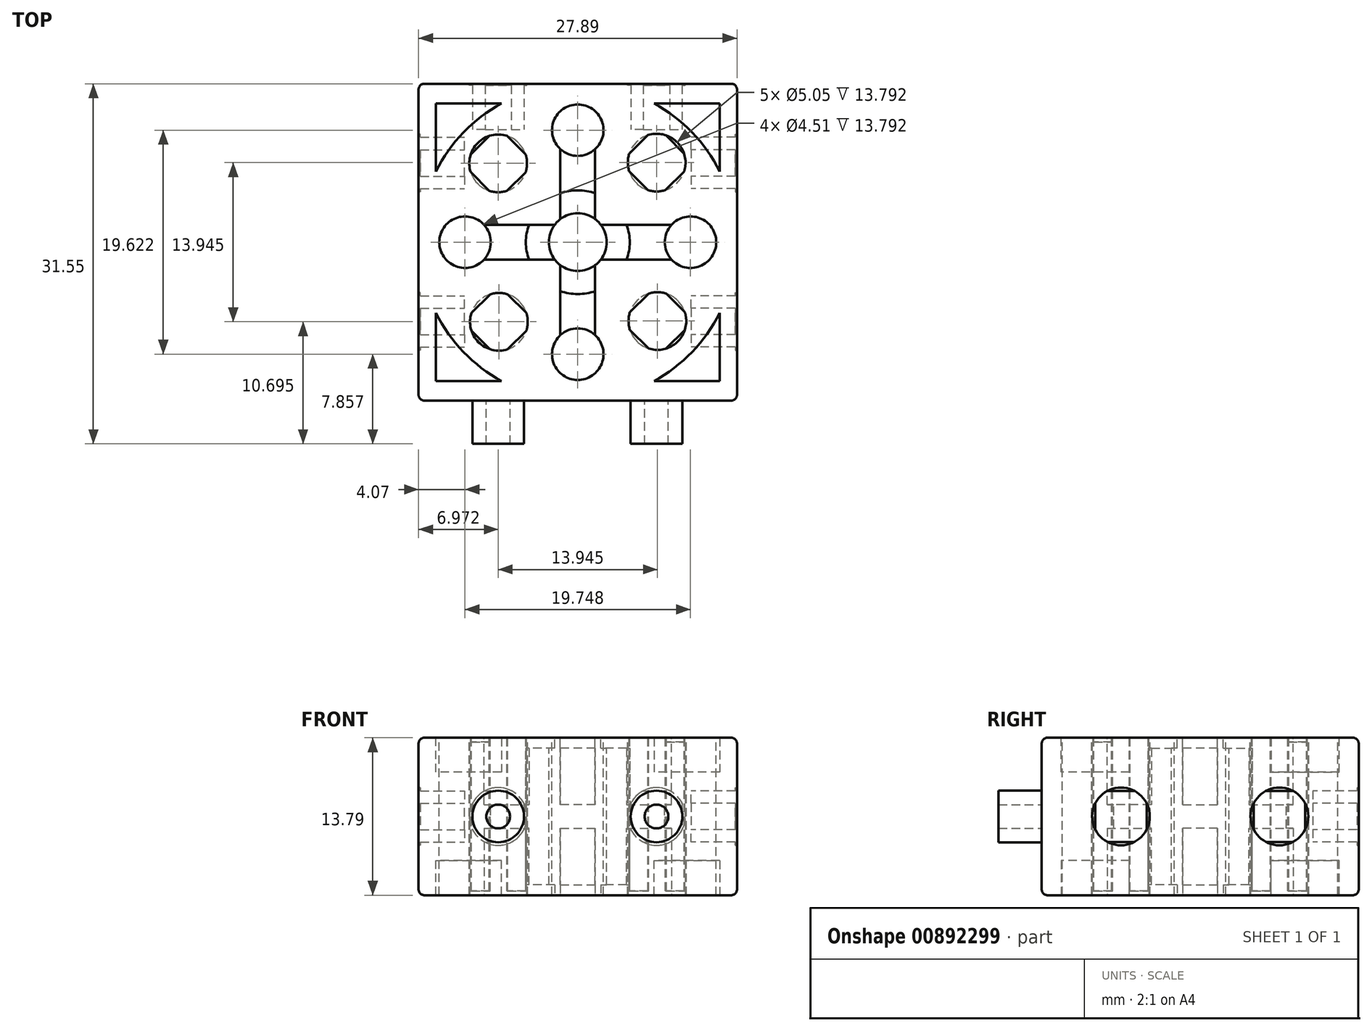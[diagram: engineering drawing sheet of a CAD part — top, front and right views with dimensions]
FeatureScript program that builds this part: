
annotation { "Feature Type Name" : "Feature", "Feature Type Description" : "" }
export const myFeature = defineFeature(function(context is Context, id is Id, definition is map)
    precondition{}
    {
        {
            var Q0;
            Q0=qCreatedBy(makeId("Top.planeOp"),FACE);
            var sketch = newSketch(context, id + "F0", { "sketchPlane" : qUnion([Q0])});
            skLineSegment(sketch, "E0.bottom", {"start": v(-12.61, 9.27) * mm, "end": v(15.28, 9.27) * mm});
            skLineSegment(sketch, "E0.top", {"start": v(-12.61, -18.5) * mm, "end": v(15.28, -18.5) * mm});
            skLineSegment(sketch, "E0.left", {"start": v(-12.61, 9.27) * mm, "end": v(-12.61, -18.5) * mm});
            skLineSegment(sketch, "E0.right", {"start": v(15.28, 9.27) * mm, "end": v(15.28, -18.5) * mm});
            skSolve(sketch);
        }
        {
            var Q0;
            Q0=qSketchRegion(id+"F0",true);
            extrude(context, id + "F1", {"entities" : qUnion([Q0]), "depth" : 13.8 * mm, "offsetDistance" : 25.4 * mm});
        }
        {
            var Q0;
            Q0=makeQuery(id+"F1.opExtrude","CAP_FACE",FACE,{"disambiguationData":[OSD([sQuery(id+"F0.wireOp",EDGE,"E0.bottom"),sQuery(id+"F0.wireOp",EDGE,"E0.top"),sQuery(id+"F0.wireOp",EDGE,"E0.left"),sQuery(id+"F0.wireOp",EDGE,"E0.right")])],"isStart":false});
            var sketch = newSketch(context, id + "F2", { "sketchPlane" : qUnion([Q0])});
            skLineSegment(sketch, "E1", {"start": v(1.33, 9.27) * mm, "end": v(1.33, -18.5) * mm, "construction": true});
            skLineSegment(sketch, "E2", {"start": v(-12.61, -4.61) * mm, "end": v(15.28, -4.61) * mm, "construction": true});
            skLineSegment(sketch, "E3.bottom", {"start": v(13.75, 7.56) * mm, "end": v(-11.09, 7.56) * mm});
            skLineSegment(sketch, "E3.top", {"start": v(13.75, -16.78) * mm, "end": v(-11.09, -16.78) * mm});
            skLineSegment(sketch, "E3.left", {"start": v(13.75, 7.56) * mm, "end": v(13.75, -16.78) * mm});
            skLineSegment(sketch, "E3.right", {"start": v(-11.09, 7.56) * mm, "end": v(-11.09, -16.78) * mm});
            skPoint(sketch, "E3.middle", {"position": v(1.33, -4.61) * mm});
            skSolve(sketch);
        }
        {
            var Q0;
            Q0=qSketchRegion(id+"F2",true);
            extrude(context, id + "F3", {"entities" : qUnion([Q0]), "operationType" : NewBodyOperationType.REMOVE, "oppositeDirection" : true, "depth" : 3.02 * mm, "offsetDistance" : 25.4 * mm});
        }
        {
            var Q0;
            Q0=makeQuery(id+"F1.opExtrude","CAP_FACE",FACE,{"disambiguationData":[OSD([sQuery(id+"F0.wireOp",EDGE,"E0.bottom"),sQuery(id+"F0.wireOp",EDGE,"E0.top"),sQuery(id+"F0.wireOp",EDGE,"E0.left"),sQuery(id+"F0.wireOp",EDGE,"E0.right")])],"isStart":true});
            var sketch = newSketch(context, id + "F4", { "sketchPlane" : qUnion([Q0])});
            skLineSegment(sketch, "E4.bottom", {"start": v(-11.09, -7.56) * mm, "end": v(13.75, -7.56) * mm});
            skLineSegment(sketch, "E4.top", {"start": v(-11.09, 16.78) * mm, "end": v(13.75, 16.78) * mm});
            skLineSegment(sketch, "E4.left", {"start": v(-11.09, -7.56) * mm, "end": v(-11.09, 16.78) * mm});
            skLineSegment(sketch, "E4.right", {"start": v(13.75, -7.56) * mm, "end": v(13.75, 16.78) * mm});
            skSolve(sketch);
        }
        {
            var Q0;
            Q0=makeQuery(id+"F4.imprint","IMPRINT",FACE,{"disambiguationData":[TD([[makeQuery(id+"F4.imprint","IMPRINT",EDGE,{"derivedFrom":sQuery(id+"F4.wireOp",EDGE,"E4.bottom")}),1.0]])]});
            extrude(context, id + "F5", {"entities" : qUnion([Q0]), "operationType" : NewBodyOperationType.REMOVE, "oppositeDirection" : true, "depth" : 3.02 * mm, "offsetDistance" : 25.4 * mm});
        }
        {
            var Q0;
            Q0=makeQuery(id+"F5.boolean.opBoolean","COPY",FACE,{"derivedFrom":makeQuery(id+"F5.opExtrude","CAP_FACE",FACE,{"disambiguationData":[OSD([sQuery(id+"F4.wireOp",EDGE,"E4.bottom"),sQuery(id+"F4.wireOp",EDGE,"E4.top"),sQuery(id+"F4.wireOp",EDGE,"E4.left"),sQuery(id+"F4.wireOp",EDGE,"E4.right")])],"isStart":false})});
            var sketch = newSketch(context, id + "F6", { "sketchPlane" : qUnion([Q0])});
            skCircle(sketch, "E5", {"center": v(1.33, 4.61) * mm, "radius": 13.88 * mm});
            skLineSegment(sketch, "E6", {"start": v(1.33, -7.56) * mm, "end": v(1.33, 16.78) * mm, "construction": true});
            skPoint(sketch, "E6.startSnap0", {"position": v(1.33, -7.56) * mm});
            skSolve(sketch);
        }
        {
            var Q0;
            {var subQ0=sQuery(id+"F6.wireOp",EDGE,"E5");var subQ1=makeQuery(id+"F5.boolean.opBoolean","COPY",EDGE,{"derivedFrom":makeQuery(id+"F5.opExtrude","CAP_EDGE",EDGE,{"disambiguationData":[OSD([sQuery(id+"F4.wireOp",EDGE,"E4.top")])],"isStart":false})});var subQ2=makeQuery(id+"F6.imprint","INTERSECT",VERTEX,{"disambiguationData":[OD(0.0)],"derivedFrom":[subQ1,subQ0]});Q0=makeQuery(id+"F6.imprint","IMPRINT",FACE,{"disambiguationData":[TD([[makeQuery(id+"F6.imprint","IMPRINT",EDGE,{"disambiguationData":[TD([[subQ2,-1.0]])],"derivedFrom":subQ0}),1.0]])]});}
            var Q1;
            {var subQ0=sQuery(id+"F6.wireOp",EDGE,"E5");var subQ1=makeQuery(id+"F5.boolean.opBoolean","COPY",EDGE,{"derivedFrom":makeQuery(id+"F5.opExtrude","CAP_EDGE",EDGE,{"disambiguationData":[OSD([sQuery(id+"F4.wireOp",EDGE,"E4.left")])],"isStart":false})});var subQ2=makeQuery(id+"F6.imprint","INTERSECT",VERTEX,{"disambiguationData":[OD(0.0)],"derivedFrom":[subQ1,subQ0]});Q1=makeQuery(id+"F6.imprint","IMPRINT",FACE,{"disambiguationData":[TD([[makeQuery(id+"F6.imprint","IMPRINT",EDGE,{"disambiguationData":[TD([[subQ2,-1.0]])],"derivedFrom":subQ0}),1.0]])]});}
            var Q2;
            {var subQ0=sQuery(id+"F6.wireOp",EDGE,"E5");var subQ1=makeQuery(id+"F5.boolean.opBoolean","COPY",EDGE,{"derivedFrom":makeQuery(id+"F5.opExtrude","CAP_EDGE",EDGE,{"disambiguationData":[OSD([sQuery(id+"F4.wireOp",EDGE,"E4.bottom")])],"isStart":false})});var subQ2=makeQuery(id+"F6.imprint","INTERSECT",VERTEX,{"disambiguationData":[OD(0.0)],"derivedFrom":[subQ1,subQ0]});Q2=makeQuery(id+"F6.imprint","IMPRINT",FACE,{"disambiguationData":[TD([[makeQuery(id+"F6.imprint","IMPRINT",EDGE,{"disambiguationData":[TD([[subQ2,-1.0]])],"derivedFrom":subQ0}),1.0]])]});}
            var Q3;
            {var subQ0=sQuery(id+"F6.wireOp",EDGE,"E5");var subQ1=makeQuery(id+"F5.boolean.opBoolean","COPY",EDGE,{"derivedFrom":makeQuery(id+"F5.opExtrude","CAP_EDGE",EDGE,{"disambiguationData":[OSD([sQuery(id+"F4.wireOp",EDGE,"E4.right")])],"isStart":false})});var subQ2=makeQuery(id+"F6.imprint","INTERSECT",VERTEX,{"disambiguationData":[OD(0.0)],"derivedFrom":[subQ1,subQ0]});Q3=makeQuery(id+"F6.imprint","IMPRINT",FACE,{"disambiguationData":[TD([[makeQuery(id+"F6.imprint","IMPRINT",EDGE,{"disambiguationData":[TD([[subQ2,1.0]])],"derivedFrom":subQ0}),1.0]])]});}
            var Q4;
            {var subQ0=sQuery(id+"F6.wireOp",EDGE,"E5");var subQ8=makeQuery(id+"F5.boolean.opBoolean","COPY",EDGE,{"derivedFrom":makeQuery(id+"F5.opExtrude","CAP_EDGE",EDGE,{"disambiguationData":[OSD([sQuery(id+"F4.wireOp",EDGE,"E4.top")])],"isStart":false})});var subQ11=makeQuery(id+"F6.imprint","INTERSECT",VERTEX,{"disambiguationData":[OD(0.0)],"derivedFrom":[subQ8,subQ0]});Q4=makeQuery(id+"F6.imprint","IMPRINT",FACE,{"disambiguationData":[TD([[makeQuery(id+"F6.imprint","IMPRINT",EDGE,{"disambiguationData":[TD([[subQ11,1.0]])],"derivedFrom":subQ0}),1.0]])]});}
            extrude(context, id + "F7", {"entities" : qUnion([Q0, Q1, Q2, Q3, Q4]), "operationType" : NewBodyOperationType.ADD, "depth" : 3.02 * mm, "offsetDistance" : 25.4 * mm});
        }
        {
            var Q0;
            Q0=makeQuery(id+"F3.boolean.opBoolean","COPY",FACE,{"derivedFrom":makeQuery(id+"F3.opExtrude","CAP_FACE",FACE,{"disambiguationData":[OSD([sQuery(id+"F2.wireOp",EDGE,"E3.bottom"),sQuery(id+"F2.wireOp",EDGE,"E3.top"),sQuery(id+"F2.wireOp",EDGE,"E3.left"),sQuery(id+"F2.wireOp",EDGE,"E3.right")])],"isStart":false})});
            var sketch = newSketch(context, id + "F8", { "sketchPlane" : qUnion([Q0])});
            skLineSegment(sketch, "E7", {"start": v(1.33, 7.56) * mm, "end": v(1.33, -16.78) * mm, "construction": true});
            skCircle(sketch, "E8", {"center": v(1.33, -4.61) * mm, "radius": 13.88 * mm});
            skSolve(sketch);
        }
        {
            var Q0;
            Q0=qSketchRegion(id+"F8",true);
            extrude(context, id + "F9", {"entities" : qUnion([Q0]), "operationType" : NewBodyOperationType.ADD, "depth" : 3.02 * mm, "offsetDistance" : 25.4 * mm});
        }
        {
            var Q0;
            Q0=makeQuery(id+"F9.boolean.opBoolean","MERGE",FACE,{"derivedFrom":[makeQuery(id+"F1.opExtrude","CAP_FACE",FACE,{"disambiguationData":[OSD([sQuery(id+"F0.wireOp",EDGE,"E0.bottom"),sQuery(id+"F0.wireOp",EDGE,"E0.top"),sQuery(id+"F0.wireOp",EDGE,"E0.left"),sQuery(id+"F0.wireOp",EDGE,"E0.right")])],"isStart":false}),makeQuery(id+"F9.opExtrude","CAP_FACE",FACE,{"disambiguationData":[OSD([sQuery(id+"F8.wireOp",EDGE,"E8")])],"isStart":false})]});
            var sketch = newSketch(context, id + "F10", { "sketchPlane" : qUnion([Q0])});
            skLineSegment(sketch, "E9", {"start": v(-12.61, -4.61) * mm, "end": v(15.28, -4.61) * mm, "construction": true});
            skLineSegment(sketch, "E10", {"start": v(1.33, 9.27) * mm, "end": v(1.33, -18.5) * mm, "construction": true});
            skCircle(sketch, "E11", {"center": v(1.33, -4.61) * mm, "radius": 2.53 * mm});
            skCircle(sketch, "E12", {"center": v(1.33, -14.42) * mm, "radius": 2.25 * mm});
            skCircle(sketch, "E13", {"center": v(1.33, 5.2) * mm, "radius": 2.25 * mm});
            skCircle(sketch, "E14", {"center": v(-8.54, -4.61) * mm, "radius": 2.25 * mm});
            skCircle(sketch, "E15", {"center": v(11.2, -4.61) * mm, "radius": 2.25 * mm});
            skCircle(sketch, "E16", {"center": v(-5.64, 2.3) * mm, "radius": 2.53 * mm});
            skCircle(sketch, "E17.1.0", {"center": v(-5.57, -11.58) * mm, "radius": 2.53 * mm});
            skCircle(sketch, "E17.2.0", {"center": v(8.3, -11.52) * mm, "radius": 2.53 * mm});
            skCircle(sketch, "E17.3.0", {"center": v(8.24, 2.36) * mm, "radius": 2.53 * mm});
            skSolve(sketch);
        }
        {
            var Q0;
            Q0=qSketchRegion(id+"F10",true);
            extrude(context, id + "F11", {"entities" : qUnion([Q0]), "operationType" : NewBodyOperationType.REMOVE, "oppositeDirection" : true, "depth" : 25.4 * mm, "offsetDistance" : 25.4 * mm});
        }
        {
            var Q0;
            Q0=makeQuery(id+"F9.boolean.opBoolean","MERGE",FACE,{"derivedFrom":[makeQuery(id+"F1.opExtrude","CAP_FACE",FACE,{"disambiguationData":[OSD([sQuery(id+"F0.wireOp",EDGE,"E0.bottom"),sQuery(id+"F0.wireOp",EDGE,"E0.top"),sQuery(id+"F0.wireOp",EDGE,"E0.left"),sQuery(id+"F0.wireOp",EDGE,"E0.right")])],"isStart":false}),makeQuery(id+"F9.opExtrude","CAP_FACE",FACE,{"disambiguationData":[OSD([sQuery(id+"F8.wireOp",EDGE,"E8")])],"isStart":false})]});
            var sketch = newSketch(context, id + "F12", { "sketchPlane" : qUnion([Q0])});
            skLineSegment(sketch, "E18", {"start": v(-12.61, -4.61) * mm, "end": v(15.28, -4.61) * mm, "construction": true});
            skLineSegment(sketch, "E19", {"start": v(1.33, 9.27) * mm, "end": v(1.33, -18.5) * mm, "construction": true});
            skLineSegment(sketch, "E20", {"start": v(-6.88, -3.09) * mm, "end": v(9.55, -3.09) * mm});
            skLineSegment(sketch, "E21", {"start": v(-6.88, -6.14) * mm, "end": v(9.55, -6.14) * mm});
            skLineSegment(sketch, "E22", {"start": v(-0.19, 3.54) * mm, "end": v(-0.19, -12.76) * mm});
            skLineSegment(sketch, "E23", {"start": v(2.86, -12.76) * mm, "end": v(2.86, 3.54) * mm});
            skLineSegment(sketch, "E24", {"start": v(-0.19, -7.96) * mm, "end": v(2.86, -7.96) * mm, "construction": true});
            skPoint(sketch, "E25", {"position": v(1.33, -7.96) * mm});
            skLineSegment(sketch, "E26", {"start": v(-2, -3.09) * mm, "end": v(-2, -6.14) * mm, "construction": true});
            skPoint(sketch, "E27", {"position": v(-2, -4.61) * mm});
            skSolve(sketch);
        }
        {
            var Q0;
            {var subQ0=sQuery(id+"F12.wireOp",EDGE,"E22");var subQ1=makeQuery(id+"F11.boolean.opBoolean","COPY",EDGE,{"derivedFrom":makeQuery(id+"F11.opExtrude","CAP_EDGE",EDGE,{"disambiguationData":[OSD([sQuery(id+"F10.wireOp",EDGE,"E13")])],"isStart":true})});var subQ2=makeQuery(id+"F12.imprint","INTERSECT",VERTEX,{"derivedFrom":[subQ1,subQ0]});Q0=makeQuery(id+"F12.imprint","IMPRINT",FACE,{"disambiguationData":[TD([[makeQuery(id+"F12.imprint","IMPRINT",EDGE,{"disambiguationData":[TD([[subQ2,-1.0]])],"derivedFrom":subQ0}),1.0]])]});}
            var Q1;
            {var subQ0=sQuery(id+"F12.wireOp",EDGE,"E22");var subQ1=makeQuery(id+"F11.boolean.opBoolean","COPY",EDGE,{"derivedFrom":makeQuery(id+"F11.opExtrude","CAP_EDGE",EDGE,{"disambiguationData":[OSD([sQuery(id+"F10.wireOp",EDGE,"E12")])],"isStart":true})});var subQ2=makeQuery(id+"F12.imprint","INTERSECT",VERTEX,{"derivedFrom":[subQ1,subQ0]});Q1=makeQuery(id+"F12.imprint","IMPRINT",FACE,{"disambiguationData":[TD([[makeQuery(id+"F12.imprint","IMPRINT",EDGE,{"disambiguationData":[TD([[subQ2,1.0]])],"derivedFrom":subQ0}),1.0]])]});}
            var Q2;
            {var subQ0=sQuery(id+"F12.wireOp",EDGE,"E20");var subQ1=makeQuery(id+"F11.boolean.opBoolean","COPY",EDGE,{"derivedFrom":makeQuery(id+"F11.opExtrude","CAP_EDGE",EDGE,{"disambiguationData":[OSD([sQuery(id+"F10.wireOp",EDGE,"E14")])],"isStart":true})});var subQ2=makeQuery(id+"F12.imprint","INTERSECT",VERTEX,{"derivedFrom":[subQ1,subQ0]});Q2=makeQuery(id+"F12.imprint","IMPRINT",FACE,{"disambiguationData":[TD([[makeQuery(id+"F12.imprint","IMPRINT",EDGE,{"disambiguationData":[TD([[subQ2,-1.0]])],"derivedFrom":subQ0}),-1.0]])]});}
            var Q3;
            {var subQ0=sQuery(id+"F12.wireOp",EDGE,"E20");var subQ1=makeQuery(id+"F11.boolean.opBoolean","COPY",EDGE,{"derivedFrom":makeQuery(id+"F11.opExtrude","CAP_EDGE",EDGE,{"disambiguationData":[OSD([sQuery(id+"F10.wireOp",EDGE,"E15")])],"isStart":true})});var subQ2=makeQuery(id+"F12.imprint","INTERSECT",VERTEX,{"derivedFrom":[subQ1,subQ0]});Q3=makeQuery(id+"F12.imprint","IMPRINT",FACE,{"disambiguationData":[TD([[makeQuery(id+"F12.imprint","IMPRINT",EDGE,{"disambiguationData":[TD([[subQ2,1.0]])],"derivedFrom":subQ0}),-1.0]])]});}
            extrude(context, id + "F13", {"entities" : qUnion([Q0, Q1, Q2, Q3]), "operationType" : NewBodyOperationType.REMOVE, "oppositeDirection" : true, "depth" : 5.87 * mm, "offsetDistance" : 25.4 * mm});
        }
        {
            var Q0;
            Q0=makeQuery(id+"F7.boolean.opBoolean","MERGE",FACE,{"derivedFrom":[makeQuery(id+"F1.opExtrude","CAP_FACE",FACE,{"disambiguationData":[OSD([sQuery(id+"F0.wireOp",EDGE,"E0.bottom"),sQuery(id+"F0.wireOp",EDGE,"E0.top"),sQuery(id+"F0.wireOp",EDGE,"E0.left"),sQuery(id+"F0.wireOp",EDGE,"E0.right")])],"isStart":true}),makeQuery(id+"F7.opExtrude","CAP_FACE",FACE,{"disambiguationData":[OSD([sQuery(id+"F6.wireOp",EDGE,"E5")])],"isStart":false})]});
            var sketch = newSketch(context, id + "F14", { "sketchPlane" : qUnion([Q0])});
            skLineSegment(sketch, "E28.0", {"start": v(2.86, 12.76) * mm, "end": v(2.86, 6.63) * mm});
            skLineSegment(sketch, "E28.1", {"start": v(3.35, 6.14) * mm, "end": v(9.55, 6.14) * mm});
            skLineSegment(sketch, "E28.2", {"start": v(3.35, 3.09) * mm, "end": v(9.55, 3.09) * mm});
            skLineSegment(sketch, "E28.3", {"start": v(2.86, 2.6) * mm, "end": v(2.86, -3.54) * mm});
            skLineSegment(sketch, "E28.4", {"start": v(-0.19, -3.54) * mm, "end": v(-0.19, 2.6) * mm});
            skLineSegment(sketch, "E28.5", {"start": v(-0.19, 6.63) * mm, "end": v(-0.19, 12.76) * mm});
            skLineSegment(sketch, "E28.6", {"start": v(-6.88, 6.14) * mm, "end": v(-0.68, 6.14) * mm});
            skLineSegment(sketch, "E28.7", {"start": v(-6.88, 3.09) * mm, "end": v(-0.68, 3.09) * mm});
            skSolve(sketch);
        }
        {
            var Q0;
            {var subQ0=sQuery(id+"F14.wireOp",EDGE,"E28.6");Q0=makeQuery(id+"F14.imprint","IMPRINT",FACE,{"disambiguationData":[TD([[makeQuery(id+"F14.imprint","IMPRINT",EDGE,{"derivedFrom":subQ0}),-1.0]])]});}
            var Q1;
            {var subQ0=sQuery(id+"F14.wireOp",EDGE,"E28.3");Q1=makeQuery(id+"F14.imprint","IMPRINT",FACE,{"disambiguationData":[TD([[makeQuery(id+"F14.imprint","IMPRINT",EDGE,{"derivedFrom":subQ0}),-1.0]])]});}
            var Q2;
            {var subQ0=sQuery(id+"F14.wireOp",EDGE,"E28.0");Q2=makeQuery(id+"F14.imprint","IMPRINT",FACE,{"disambiguationData":[TD([[makeQuery(id+"F14.imprint","IMPRINT",EDGE,{"derivedFrom":subQ0}),-1.0]])]});}
            var Q3;
            {var subQ0=sQuery(id+"F14.wireOp",EDGE,"E28.1");Q3=makeQuery(id+"F14.imprint","IMPRINT",FACE,{"disambiguationData":[TD([[makeQuery(id+"F14.imprint","IMPRINT",EDGE,{"derivedFrom":subQ0}),-1.0]])]});}
            extrude(context, id + "F15", {"entities" : qUnion([Q0, Q1, Q2, Q3]), "operationType" : NewBodyOperationType.REMOVE, "oppositeDirection" : true, "depth" : 5.87 * mm, "offsetDistance" : 25.4 * mm});
        }
        {
            var Q0;
            Q0=makeQuery(id+"F15.boolean.opBoolean","COPY",FACE,{"derivedFrom":makeQuery(id+"F15.opExtrude","CAP_FACE",FACE,{"disambiguationData":[OSD([sQuery(id+"F0.wireOp",EDGE,"E0.bottom"),sQuery(id+"F0.wireOp",EDGE,"E0.top"),sQuery(id+"F0.wireOp",EDGE,"E0.left"),sQuery(id+"F0.wireOp",EDGE,"E0.right"),sQuery(id+"F6.wireOp",EDGE,"E5"),sQuery(id+"F10.wireOp",EDGE,"E11"),sQuery(id+"F10.wireOp",EDGE,"E13"),sQuery(id+"F14.wireOp",EDGE,"E28.3"),sQuery(id+"F14.wireOp",EDGE,"E28.4")])],"isStart":false})});
            var sketch = newSketch(context, id + "F16", { "sketchPlane" : qUnion([Q0])});
            skCircle(sketch, "E29", {"center": v(1.33, 4.61) * mm, "radius": 4.55 * mm});
            skCircle(sketch, "E30", {"center": v(1.33, 4.61) * mm, "radius": 2.53 * mm});
            skSolve(sketch);
        }
        {
            var Q0;
            {var subQ5=sQuery(id+"F16.wireOp",EDGE,"E30");Q0=makeQuery(id+"F16.imprint","IMPRINT",FACE,{"disambiguationData":[TD([[makeQuery(id+"F16.imprint","IMPRINT",EDGE,{"disambiguationData":[OD(1.0)],"derivedFrom":subQ5}),-1.0]])]});}
            var Q1;
            {var subQ5=sQuery(id+"F16.wireOp",EDGE,"E30");Q1=makeQuery(id+"F16.imprint","IMPRINT",FACE,{"disambiguationData":[TD([[makeQuery(id+"F16.imprint","IMPRINT",EDGE,{"disambiguationData":[OD(0.0)],"derivedFrom":subQ5}),1.0]])]});}
            extrude(context, id + "F17", {"entities" : qUnion([Q0, Q1]), "operationType" : NewBodyOperationType.ADD, "depth" : 4.95 * mm, "offsetDistance" : 25.4 * mm});
        }
        {
            var Q0;
            Q0=makeQuery(id+"F13.boolean.opBoolean","COPY",FACE,{"derivedFrom":makeQuery(id+"F13.opExtrude","CAP_FACE",FACE,{"disambiguationData":[OSD([sQuery(id+"F10.wireOp",EDGE,"E11"),sQuery(id+"F10.wireOp",EDGE,"E12"),sQuery(id+"F12.wireOp",EDGE,"E22"),sQuery(id+"F12.wireOp",EDGE,"E23")])],"isStart":false})});
            var sketch = newSketch(context, id + "F18", { "sketchPlane" : qUnion([Q0])});
            skCircle(sketch, "E31", {"center": v(1.33, -4.61) * mm, "radius": 4.55 * mm});
            skCircle(sketch, "E32", {"center": v(1.33, -4.61) * mm, "radius": 2.53 * mm});
            skSolve(sketch);
        }
        {
            var Q0;
            {var subQ0=sQuery(id+"F18.wireOp",EDGE,"E31");var subQ1=sQuery(id+"F12.wireOp",EDGE,"E22");var subQ2=makeQuery(id+"F11.boolean.opBoolean","COPY",EDGE,{"derivedFrom":makeQuery(id+"F11.opExtrude","CAP_EDGE",EDGE,{"disambiguationData":[OSD([sQuery(id+"F10.wireOp",EDGE,"E12")])],"isStart":true})});var subQ4=makeQuery(id+"F13.boolean.opBoolean","COPY",EDGE,{"derivedFrom":makeQuery(id+"F13.opExtrude","CAP_EDGE",EDGE,{"disambiguationData":[OSD([subQ1]),TDD([makeQuery(id+"F12.imprint","IMPRINT",EDGE,{"disambiguationData":[TD([[makeQuery(id+"F12.imprint","INTERSECT",VERTEX,{"derivedFrom":[subQ2,subQ1]}),1.0]])],"derivedFrom":subQ1})])],"isStart":false})});var subQ5=makeQuery(id+"F18.imprint","INTERSECT",VERTEX,{"derivedFrom":[subQ4,subQ0]});Q0=makeQuery(id+"F18.imprint","IMPRINT",FACE,{"disambiguationData":[TD([[makeQuery(id+"F18.imprint","IMPRINT",EDGE,{"disambiguationData":[TD([[subQ5,1.0]])],"derivedFrom":subQ0}),1.0]])]});}
            var Q1;
            {var subQ0=sQuery(id+"F18.wireOp",EDGE,"E31");var subQ1=sQuery(id+"F12.wireOp",EDGE,"E22");var subQ2=makeQuery(id+"F11.boolean.opBoolean","COPY",EDGE,{"derivedFrom":makeQuery(id+"F11.opExtrude","CAP_EDGE",EDGE,{"disambiguationData":[OSD([sQuery(id+"F10.wireOp",EDGE,"E12")])],"isStart":true})});var subQ4=makeQuery(id+"F13.boolean.opBoolean","COPY",EDGE,{"derivedFrom":makeQuery(id+"F13.opExtrude","CAP_EDGE",EDGE,{"disambiguationData":[OSD([subQ1]),TDD([makeQuery(id+"F12.imprint","IMPRINT",EDGE,{"disambiguationData":[TD([[makeQuery(id+"F12.imprint","INTERSECT",VERTEX,{"derivedFrom":[subQ2,subQ1]}),1.0]])],"derivedFrom":subQ1})])],"isStart":false})});var subQ5=makeQuery(id+"F18.imprint","INTERSECT",VERTEX,{"derivedFrom":[subQ4,subQ0]});Q1=makeQuery(id+"F18.imprint","IMPRINT",FACE,{"disambiguationData":[TD([[makeQuery(id+"F18.imprint","IMPRINT",EDGE,{"disambiguationData":[TD([[subQ5,-1.0]])],"derivedFrom":subQ0}),1.0]])]});}
            extrude(context, id + "F19", {"entities" : qUnion([Q0, Q1]), "operationType" : NewBodyOperationType.ADD, "depth" : 4.95 * mm, "offsetDistance" : 25.4 * mm});
        }
        {
            var Q0;
            Q0=makeQuery(id+"F1.opExtrude","SWEPT_FACE",FACE,{"disambiguationData":[OSD([sQuery(id+"F0.wireOp",EDGE,"E0.top")])]});
            var sketch = newSketch(context, id + "F20", { "sketchPlane" : qUnion([Q0])});
            skLineSegment(sketch, "E33", {"start": v(15.28, 6.9) * mm, "end": v(-12.61, 6.9) * mm, "construction": true});
            skCircle(sketch, "E34", {"center": v(8.23, 6.9) * mm, "radius": 2.26 * mm});
            skCircle(sketch, "E35", {"center": v(-5.64, 6.9) * mm, "radius": 2.26 * mm});
            skLineSegment(sketch, "E36", {"start": v(1.33, 0) * mm, "end": v(1.33, 13.8) * mm, "construction": true});
            skPoint(sketch, "E37", {"position": v(1.33, 6.9) * mm});
            skLineSegment(sketch, "E38", {"start": v(1.33, 0) * mm, "end": v(15.28, 0) * mm, "construction": true});
            skLineSegment(sketch, "E39", {"start": v(15.28, 0) * mm, "end": v(8.3, 0) * mm});
            skLineSegment(sketch, "E40", {"start": v(8.3, 0) * mm, "end": v(8.3, 13.8) * mm, "construction": true});
            skLineSegment(sketch, "E41", {"start": v(1.33, 0) * mm, "end": v(-12.61, 0) * mm, "construction": true});
            skLineSegment(sketch, "E42", {"start": v(-5.64, 0) * mm, "end": v(-5.64, 13.8) * mm, "construction": true});
            skCircle(sketch, "E43", {"center": v(8.23, 6.9) * mm, "radius": 1.04 * mm});
            skCircle(sketch, "E44", {"center": v(-5.64, 6.9) * mm, "radius": 1.04 * mm});
            skLineSegment(sketch, "E45.0", {"start": v(-12.61, 13.8) * mm, "end": v(-12.61, 0) * mm});
            skSolve(sketch);
        }
        {
            var Q0;
            Q0=makeQuery(id+"F20.imprint","IMPRINT",FACE,{"disambiguationData":[TD([[makeQuery(id+"F20.imprint","IMPRINT",EDGE,{"derivedFrom":sQuery(id+"F20.wireOp",EDGE,"E34")}),1.0]])]});
            var Q1;
            Q1=makeQuery(id+"F20.imprint","IMPRINT",FACE,{"disambiguationData":[TD([[makeQuery(id+"F20.imprint","IMPRINT",EDGE,{"derivedFrom":sQuery(id+"F20.wireOp",EDGE,"E35")}),1.0]])]});
            extrude(context, id + "F21", {"entities" : qUnion([Q0, Q1]), "operationType" : NewBodyOperationType.ADD, "depth" : 3.78 * mm, "offsetDistance" : 25.4 * mm});
        }
        {
            var Q0;
            Q0=makeQuery(id+"F1.opExtrude","SWEPT_FACE",FACE,{"disambiguationData":[OSD([sQuery(id+"F0.wireOp",EDGE,"E0.bottom")])]});
            var sketch = newSketch(context, id + "F22", { "sketchPlane" : qUnion([Q0])});
            skCircle(sketch, "E46.0", {"center": v(-8.23, 6.9) * mm, "radius": 2.26 * mm, "construction": true});
            skCircle(sketch, "E46.1", {"center": v(5.64, 6.9) * mm, "radius": 2.26 * mm, "construction": true});
            skCircle(sketch, "E47", {"center": v(-8.23, 6.9) * mm, "radius": 2.53 * mm});
            skCircle(sketch, "E48", {"center": v(5.64, 6.9) * mm, "radius": 2.53 * mm});
            skSolve(sketch);
        }
        {
            var Q0;
            Q0=qSketchRegion(id+"F22",true);
            extrude(context, id + "F23", {"entities" : qUnion([Q0]), "operationType" : NewBodyOperationType.REMOVE, "oppositeDirection" : true, "depth" : 4 * mm, "offsetDistance" : 25.4 * mm});
        }
        {
            var Q0;
            Q0=makeQuery(id+"F1.opExtrude","SWEPT_FACE",FACE,{"disambiguationData":[OSD([sQuery(id+"F0.wireOp",EDGE,"E0.right")])]});
            var sketch = newSketch(context, id + "F24", { "sketchPlane" : qUnion([Q0])});
            skLineSegment(sketch, "E49", {"start": v(9.27, 6.9) * mm, "end": v(-18.5, 6.9) * mm, "construction": true});
            skLineSegment(sketch, "E50", {"start": v(-4.61, 13.8) * mm, "end": v(-4.61, 0) * mm});
            skLineSegment(sketch, "E51", {"start": v(-4.61, 13.8) * mm, "end": v(9.27, 13.8) * mm, "construction": true});
            skLineSegment(sketch, "E52", {"start": v(-4.61, 13.8) * mm, "end": v(-18.5, 13.8) * mm, "construction": true});
            skLineSegment(sketch, "E53", {"start": v(-11.55, 13.8) * mm, "end": v(-11.55, 0) * mm, "construction": true});
            skLineSegment(sketch, "E54", {"start": v(2.33, 13.8) * mm, "end": v(2.33, 0) * mm, "construction": true});
            skPoint(sketch, "E55", {"position": v(-11.55, 6.9) * mm});
            skPoint(sketch, "E56", {"position": v(2.33, 6.9) * mm});
            skCircle(sketch, "E57", {"center": v(-11.55, 6.9) * mm, "radius": 2.53 * mm});
            skCircle(sketch, "E58", {"center": v(2.33, 6.9) * mm, "radius": 2.53 * mm});
            skSolve(sketch);
        }
        {
            var Q0;
            Q0=qSketchRegion(id+"F24",true);
            extrude(context, id + "F25", {"entities" : qUnion([Q0]), "operationType" : NewBodyOperationType.REMOVE, "oppositeDirection" : true, "depth" : 4 * mm, "offsetDistance" : 25.4 * mm});
        }
        {
            var Q0;
            Q0=makeQuery(id+"F1.opExtrude","SWEPT_FACE",FACE,{"disambiguationData":[OSD([sQuery(id+"F0.wireOp",EDGE,"E0.left")])]});
            var sketch = newSketch(context, id + "F26", { "sketchPlane" : qUnion([Q0])});
            skCircle(sketch, "E59.0", {"center": v(-2.33, 6.9) * mm, "radius": 2.53 * mm});
            skCircle(sketch, "E59.1", {"center": v(11.55, 6.9) * mm, "radius": 2.53 * mm});
            skSolve(sketch);
        }
        {
            var Q0;
            Q0=qSketchRegion(id+"F26",true);
            extrude(context, id + "F27", {"entities" : qUnion([Q0]), "operationType" : NewBodyOperationType.REMOVE, "oppositeDirection" : true, "depth" : 4 * mm, "offsetDistance" : 25.4 * mm});
        }
        {
            var Q0;
            Q0=makeQuery(id+"F23.boolean.opBoolean","COPY",FACE,{"derivedFrom":makeQuery(id+"F23.opExtrude","CAP_FACE",FACE,{"disambiguationData":[OSD([sQuery(id+"F22.wireOp",EDGE,"E47")])],"isStart":false})});
            var sketch = newSketch(context, id + "F28", { "sketchPlane" : qUnion([Q0])});
            skLineSegment(sketch, "E60.bottom", {"start": v(-5.98, 9.14) * mm, "end": v(-10.48, 9.14) * mm});
            skLineSegment(sketch, "E60.top", {"start": v(-5.98, 4.65) * mm, "end": v(-10.48, 4.65) * mm});
            skLineSegment(sketch, "E60.left", {"start": v(-5.98, 9.14) * mm, "end": v(-5.98, 4.65) * mm});
            skLineSegment(sketch, "E60.right", {"start": v(-10.48, 9.14) * mm, "end": v(-10.48, 4.65) * mm});
            skPoint(sketch, "E60.middle", {"position": v(-8.23, 6.9) * mm});
            skLineSegment(sketch, "E61.bottom", {"start": v(7.89, 9.14) * mm, "end": v(3.4, 9.14) * mm});
            skLineSegment(sketch, "E61.top", {"start": v(7.89, 4.65) * mm, "end": v(3.4, 4.65) * mm});
            skLineSegment(sketch, "E61.left", {"start": v(7.89, 9.14) * mm, "end": v(7.89, 4.65) * mm});
            skLineSegment(sketch, "E61.right", {"start": v(3.4, 9.14) * mm, "end": v(3.4, 4.65) * mm});
            skPoint(sketch, "E61.middle", {"position": v(5.64, 6.9) * mm});
            skCircle(sketch, "E62.0", {"center": v(-8.23, 6.9) * mm, "radius": 2.53 * mm});
            skCircle(sketch, "E63.0", {"center": v(5.64, 6.9) * mm, "radius": 2.53 * mm});
            skSolve(sketch);
        }
        {
            var Q0;
            {var subQ0=sQuery(id+"F28.wireOp",EDGE,"E62.0");var subQ1=sQuery(id+"F28.wireOp",EDGE,"E60.right");var subQ2=makeQuery(id+"F28.imprint","INTERSECT",VERTEX,{"disambiguationData":[OD(0.0)],"derivedFrom":[subQ1,subQ0]});Q0=makeQuery(id+"F28.imprint","IMPRINT",FACE,{"disambiguationData":[TD([[makeQuery(id+"F28.imprint","IMPRINT",EDGE,{"disambiguationData":[TD([[subQ2,-1.0]])],"derivedFrom":subQ1}),-1.0]])]});}
            var Q1;
            {var subQ0=sQuery(id+"F28.wireOp",EDGE,"E62.0");var subQ1=sQuery(id+"F28.wireOp",EDGE,"E60.top");var subQ2=makeQuery(id+"F28.imprint","INTERSECT",VERTEX,{"disambiguationData":[OD(0.0)],"derivedFrom":[subQ1,subQ0]});Q1=makeQuery(id+"F28.imprint","IMPRINT",FACE,{"disambiguationData":[TD([[makeQuery(id+"F28.imprint","IMPRINT",EDGE,{"disambiguationData":[TD([[subQ2,-1.0]])],"derivedFrom":subQ1}),1.0]])]});}
            var Q2;
            {var subQ0=sQuery(id+"F28.wireOp",EDGE,"E62.0");var subQ1=sQuery(id+"F28.wireOp",EDGE,"E60.left");var subQ2=makeQuery(id+"F28.imprint","INTERSECT",VERTEX,{"disambiguationData":[OD(0.0)],"derivedFrom":[subQ1,subQ0]});Q2=makeQuery(id+"F28.imprint","IMPRINT",FACE,{"disambiguationData":[TD([[makeQuery(id+"F28.imprint","IMPRINT",EDGE,{"disambiguationData":[TD([[subQ2,-1.0]])],"derivedFrom":subQ1}),1.0]])]});}
            var Q3;
            {var subQ0=sQuery(id+"F28.wireOp",EDGE,"E62.0");var subQ1=sQuery(id+"F28.wireOp",EDGE,"E60.bottom");var subQ2=makeQuery(id+"F28.imprint","INTERSECT",VERTEX,{"disambiguationData":[OD(0.0)],"derivedFrom":[subQ1,subQ0]});Q3=makeQuery(id+"F28.imprint","IMPRINT",FACE,{"disambiguationData":[TD([[makeQuery(id+"F28.imprint","IMPRINT",EDGE,{"disambiguationData":[TD([[subQ2,-1.0]])],"derivedFrom":subQ1}),-1.0]])]});}
            var Q4;
            {var subQ0=sQuery(id+"F28.wireOp",EDGE,"E63.0");var subQ1=sQuery(id+"F28.wireOp",EDGE,"E61.bottom");var subQ2=makeQuery(id+"F28.imprint","INTERSECT",VERTEX,{"disambiguationData":[OD(0.0)],"derivedFrom":[subQ1,subQ0]});Q4=makeQuery(id+"F28.imprint","IMPRINT",FACE,{"disambiguationData":[TD([[makeQuery(id+"F28.imprint","IMPRINT",EDGE,{"disambiguationData":[TD([[subQ2,-1.0]])],"derivedFrom":subQ1}),-1.0]])]});}
            var Q5;
            {var subQ0=sQuery(id+"F28.wireOp",EDGE,"E63.0");var subQ1=sQuery(id+"F28.wireOp",EDGE,"E61.left");var subQ2=makeQuery(id+"F28.imprint","INTERSECT",VERTEX,{"disambiguationData":[OD(0.0)],"derivedFrom":[subQ1,subQ0]});Q5=makeQuery(id+"F28.imprint","IMPRINT",FACE,{"disambiguationData":[TD([[makeQuery(id+"F28.imprint","IMPRINT",EDGE,{"disambiguationData":[TD([[subQ2,-1.0]])],"derivedFrom":subQ1}),1.0]])]});}
            var Q6;
            {var subQ0=sQuery(id+"F28.wireOp",EDGE,"E63.0");var subQ1=sQuery(id+"F28.wireOp",EDGE,"E61.right");var subQ2=makeQuery(id+"F28.imprint","INTERSECT",VERTEX,{"disambiguationData":[OD(0.0)],"derivedFrom":[subQ1,subQ0]});Q6=makeQuery(id+"F28.imprint","IMPRINT",FACE,{"disambiguationData":[TD([[makeQuery(id+"F28.imprint","IMPRINT",EDGE,{"disambiguationData":[TD([[subQ2,-1.0]])],"derivedFrom":subQ1}),-1.0]])]});}
            var Q7;
            {var subQ0=sQuery(id+"F28.wireOp",EDGE,"E63.0");var subQ1=sQuery(id+"F28.wireOp",EDGE,"E61.top");var subQ2=makeQuery(id+"F28.imprint","INTERSECT",VERTEX,{"disambiguationData":[OD(0.0)],"derivedFrom":[subQ1,subQ0]});Q7=makeQuery(id+"F28.imprint","IMPRINT",FACE,{"disambiguationData":[TD([[makeQuery(id+"F28.imprint","IMPRINT",EDGE,{"disambiguationData":[TD([[subQ2,-1.0]])],"derivedFrom":subQ1}),1.0]])]});}
            extrude(context, id + "F29", {"entities" : qUnion([Q0, Q1, Q2, Q3, Q4, Q5, Q6, Q7]), "operationType" : NewBodyOperationType.ADD, "depth" : 3.86 * mm, "offsetDistance" : 25.4 * mm});
        }
        {
            var Q0;
            Q0=makeQuery(id+"F25.boolean.opBoolean","COPY",FACE,{"derivedFrom":makeQuery(id+"F25.opExtrude","CAP_FACE",FACE,{"disambiguationData":[OSD([sQuery(id+"F24.wireOp",EDGE,"E57")])],"isStart":false})});
            var sketch = newSketch(context, id + "F30", { "sketchPlane" : qUnion([Q0])});
            skLineSegment(sketch, "E64.bottom", {"start": v(-9.3, 9.14) * mm, "end": v(-13.8, 9.14) * mm});
            skLineSegment(sketch, "E64.top", {"start": v(-9.3, 4.65) * mm, "end": v(-13.8, 4.65) * mm});
            skLineSegment(sketch, "E64.left", {"start": v(-9.3, 9.14) * mm, "end": v(-9.3, 4.65) * mm});
            skLineSegment(sketch, "E64.right", {"start": v(-13.8, 9.14) * mm, "end": v(-13.8, 4.65) * mm});
            skPoint(sketch, "E64.middle", {"position": v(-11.55, 6.9) * mm});
            skLineSegment(sketch, "E65.bottom", {"start": v(4.58, 9.14) * mm, "end": v(0.08, 9.14) * mm});
            skLineSegment(sketch, "E65.top", {"start": v(4.58, 4.65) * mm, "end": v(0.08, 4.65) * mm});
            skLineSegment(sketch, "E65.left", {"start": v(4.58, 9.14) * mm, "end": v(4.58, 4.65) * mm});
            skLineSegment(sketch, "E65.right", {"start": v(0.08, 9.14) * mm, "end": v(0.08, 4.65) * mm});
            skPoint(sketch, "E65.middle", {"position": v(2.33, 6.9) * mm});
            skCircle(sketch, "E66.0", {"center": v(-11.55, 6.9) * mm, "radius": 2.53 * mm});
            skCircle(sketch, "E66.1", {"center": v(2.33, 6.9) * mm, "radius": 2.53 * mm});
            skSolve(sketch);
        }
        {
            var Q0;
            {var subQ0=sQuery(id+"F30.wireOp",EDGE,"E66.0");var subQ1=sQuery(id+"F30.wireOp",EDGE,"E64.bottom");var subQ2=makeQuery(id+"F30.imprint","INTERSECT",VERTEX,{"disambiguationData":[OD(0.0)],"derivedFrom":[subQ1,subQ0]});Q0=makeQuery(id+"F30.imprint","IMPRINT",FACE,{"disambiguationData":[TD([[makeQuery(id+"F30.imprint","IMPRINT",EDGE,{"disambiguationData":[TD([[subQ2,-1.0]])],"derivedFrom":subQ1}),-1.0]])]});}
            var Q1;
            {var subQ0=sQuery(id+"F30.wireOp",EDGE,"E66.0");var subQ1=sQuery(id+"F30.wireOp",EDGE,"E64.right");var subQ2=makeQuery(id+"F30.imprint","INTERSECT",VERTEX,{"disambiguationData":[OD(0.0)],"derivedFrom":[subQ1,subQ0]});Q1=makeQuery(id+"F30.imprint","IMPRINT",FACE,{"disambiguationData":[TD([[makeQuery(id+"F30.imprint","IMPRINT",EDGE,{"disambiguationData":[TD([[subQ2,-1.0]])],"derivedFrom":subQ1}),-1.0]])]});}
            var Q2;
            {var subQ0=sQuery(id+"F30.wireOp",EDGE,"E66.0");var subQ1=sQuery(id+"F30.wireOp",EDGE,"E64.left");var subQ2=makeQuery(id+"F30.imprint","INTERSECT",VERTEX,{"disambiguationData":[OD(0.0)],"derivedFrom":[subQ1,subQ0]});Q2=makeQuery(id+"F30.imprint","IMPRINT",FACE,{"disambiguationData":[TD([[makeQuery(id+"F30.imprint","IMPRINT",EDGE,{"disambiguationData":[TD([[subQ2,-1.0]])],"derivedFrom":subQ1}),1.0]])]});}
            var Q3;
            {var subQ0=sQuery(id+"F30.wireOp",EDGE,"E66.0");var subQ1=sQuery(id+"F30.wireOp",EDGE,"E64.top");var subQ2=makeQuery(id+"F30.imprint","INTERSECT",VERTEX,{"disambiguationData":[OD(0.0)],"derivedFrom":[subQ1,subQ0]});Q3=makeQuery(id+"F30.imprint","IMPRINT",FACE,{"disambiguationData":[TD([[makeQuery(id+"F30.imprint","IMPRINT",EDGE,{"disambiguationData":[TD([[subQ2,-1.0]])],"derivedFrom":subQ1}),1.0]])]});}
            var Q4;
            {var subQ0=sQuery(id+"F30.wireOp",EDGE,"E66.1");var subQ1=sQuery(id+"F30.wireOp",EDGE,"E65.bottom");var subQ2=makeQuery(id+"F30.imprint","INTERSECT",VERTEX,{"disambiguationData":[OD(0.0)],"derivedFrom":[subQ1,subQ0]});Q4=makeQuery(id+"F30.imprint","IMPRINT",FACE,{"disambiguationData":[TD([[makeQuery(id+"F30.imprint","IMPRINT",EDGE,{"disambiguationData":[TD([[subQ2,-1.0]])],"derivedFrom":subQ1}),-1.0]])]});}
            var Q5;
            {var subQ0=sQuery(id+"F30.wireOp",EDGE,"E66.1");var subQ1=sQuery(id+"F30.wireOp",EDGE,"E65.left");var subQ2=makeQuery(id+"F30.imprint","INTERSECT",VERTEX,{"disambiguationData":[OD(0.0)],"derivedFrom":[subQ1,subQ0]});Q5=makeQuery(id+"F30.imprint","IMPRINT",FACE,{"disambiguationData":[TD([[makeQuery(id+"F30.imprint","IMPRINT",EDGE,{"disambiguationData":[TD([[subQ2,-1.0]])],"derivedFrom":subQ1}),1.0]])]});}
            var Q6;
            {var subQ0=sQuery(id+"F30.wireOp",EDGE,"E66.1");var subQ1=sQuery(id+"F30.wireOp",EDGE,"E65.right");var subQ2=makeQuery(id+"F30.imprint","INTERSECT",VERTEX,{"disambiguationData":[OD(0.0)],"derivedFrom":[subQ1,subQ0]});Q6=makeQuery(id+"F30.imprint","IMPRINT",FACE,{"disambiguationData":[TD([[makeQuery(id+"F30.imprint","IMPRINT",EDGE,{"disambiguationData":[TD([[subQ2,-1.0]])],"derivedFrom":subQ1}),-1.0]])]});}
            var Q7;
            {var subQ0=sQuery(id+"F30.wireOp",EDGE,"E66.1");var subQ1=sQuery(id+"F30.wireOp",EDGE,"E65.top");var subQ2=makeQuery(id+"F30.imprint","INTERSECT",VERTEX,{"disambiguationData":[OD(0.0)],"derivedFrom":[subQ1,subQ0]});Q7=makeQuery(id+"F30.imprint","IMPRINT",FACE,{"disambiguationData":[TD([[makeQuery(id+"F30.imprint","IMPRINT",EDGE,{"disambiguationData":[TD([[subQ2,-1.0]])],"derivedFrom":subQ1}),1.0]])]});}
            extrude(context, id + "F31", {"entities" : qUnion([Q0, Q1, Q2, Q3, Q4, Q5, Q6, Q7]), "operationType" : NewBodyOperationType.ADD, "depth" : 3.86 * mm, "offsetDistance" : 25.4 * mm});
        }
        {
            var Q0;
            Q0=makeQuery(id+"F27.boolean.opBoolean","COPY",FACE,{"derivedFrom":makeQuery(id+"F27.opExtrude","CAP_FACE",FACE,{"disambiguationData":[OSD([sQuery(id+"F26.wireOp",EDGE,"E59.0")])],"isStart":false})});
            var sketch = newSketch(context, id + "F32", { "sketchPlane" : qUnion([Q0])});
            skLineSegment(sketch, "E67.0.0", {"start": v(-1.17, 9.14) * mm, "end": v(-3.48, 9.14) * mm});
            skArc(sketch, "E67.0.1", {"start": v(-3.48, 9.14) * mm, "mid": v(-2.33, 9.42) * mm, "end": v(-1.17, 9.14) * mm});
            skLineSegment(sketch, "E67.1.0", {"start": v(-4.58, 8.05) * mm, "end": v(-4.58, 5.74) * mm});
            skArc(sketch, "E67.1.1", {"start": v(-4.58, 5.74) * mm, "mid": v(-4.86, 6.9) * mm, "end": v(-4.58, 8.05) * mm});
            skLineSegment(sketch, "E67.2.0", {"start": v(-3.48, 4.65) * mm, "end": v(-1.17, 4.65) * mm});
            skArc(sketch, "E67.2.1", {"start": v(-1.17, 4.65) * mm, "mid": v(-2.33, 4.37) * mm, "end": v(-3.48, 4.65) * mm});
            skLineSegment(sketch, "E67.3.0", {"start": v(-0.08, 5.74) * mm, "end": v(-0.08, 8.05) * mm});
            skArc(sketch, "E67.3.1", {"start": v(-0.08, 8.05) * mm, "mid": v(0.2, 6.9) * mm, "end": v(-0.08, 5.74) * mm});
            skLineSegment(sketch, "E67.4.0", {"start": v(12.7, 9.14) * mm, "end": v(10.4, 9.14) * mm});
            skArc(sketch, "E67.4.1", {"start": v(10.4, 9.14) * mm, "mid": v(11.55, 9.42) * mm, "end": v(12.7, 9.14) * mm});
            skArc(sketch, "E67.5.0", {"start": v(9.3, 5.74) * mm, "mid": v(9.03, 6.9) * mm, "end": v(9.3, 8.05) * mm});
            skLineSegment(sketch, "E67.5.1", {"start": v(9.3, 8.05) * mm, "end": v(9.3, 5.74) * mm});
            skArc(sketch, "E67.6.0", {"start": v(12.7, 4.65) * mm, "mid": v(11.55, 4.37) * mm, "end": v(10.4, 4.65) * mm});
            skLineSegment(sketch, "E67.6.1", {"start": v(10.4, 4.65) * mm, "end": v(12.7, 4.65) * mm});
            skLineSegment(sketch, "E67.7.0", {"start": v(13.8, 5.74) * mm, "end": v(13.8, 8.05) * mm});
            skArc(sketch, "E67.7.1", {"start": v(13.8, 8.05) * mm, "mid": v(14.08, 6.9) * mm, "end": v(13.8, 5.74) * mm});
            skSolve(sketch);
        }
        {
            var Q0;
            Q0=qSketchRegion(id+"F32",true);
            extrude(context, id + "F33", {"entities" : qUnion([Q0]), "operationType" : NewBodyOperationType.ADD, "depth" : 3.86 * mm, "offsetDistance" : 25.4 * mm});
        }
        {
            var Q0;
            Q0=makeQuery(id+"F9.boolean.opBoolean","MERGE",FACE,{"derivedFrom":[makeQuery(id+"F1.opExtrude","CAP_FACE",FACE,{"disambiguationData":[OSD([sQuery(id+"F0.wireOp",EDGE,"E0.bottom"),sQuery(id+"F0.wireOp",EDGE,"E0.top"),sQuery(id+"F0.wireOp",EDGE,"E0.left"),sQuery(id+"F0.wireOp",EDGE,"E0.right")])],"isStart":false}),makeQuery(id+"F9.opExtrude","CAP_FACE",FACE,{"disambiguationData":[OSD([sQuery(id+"F8.wireOp",EDGE,"E8")])],"isStart":false})]});
            var sketch = newSketch(context, id + "F34", { "sketchPlane" : qUnion([Q0])});
            skLineSegment(sketch, "E68", {"start": v(-12.61, -18.5) * mm, "end": v(15.28, 9.27) * mm, "construction": true});
            skLineSegment(sketch, "E69", {"start": v(-5.58, -14.76) * mm, "end": v(-8.75, -11.58) * mm});
            skLineSegment(sketch, "E70", {"start": v(-8.75, -11.58) * mm, "end": v(-5.57, -8.4) * mm});
            skLineSegment(sketch, "E71", {"start": v(-5.57, -8.4) * mm, "end": v(-2.4, -11.6) * mm});
            skLineSegment(sketch, "E72", {"start": v(-2.4, -11.6) * mm, "end": v(-5.58, -14.76) * mm});
            skLineSegment(sketch, "E73", {"start": v(-7.16, -10) * mm, "end": v(-3.99, -13.18) * mm});
            skPoint(sketch, "E74", {"position": v(-5.57, -11.58) * mm});
            skLineSegment(sketch, "E75.1.0", {"start": v(11.49, -11.53) * mm, "end": v(8.3, -14.7) * mm});
            skLineSegment(sketch, "E75.1.1", {"start": v(8.31, -8.34) * mm, "end": v(11.49, -11.53) * mm});
            skLineSegment(sketch, "E75.1.2", {"start": v(5.13, -11.51) * mm, "end": v(8.31, -8.34) * mm});
            skLineSegment(sketch, "E75.1.3", {"start": v(8.3, -14.7) * mm, "end": v(5.13, -11.51) * mm});
            skLineSegment(sketch, "E75.2.0", {"start": v(8.25, 5.54) * mm, "end": v(11.42, 2.35) * mm});
            skLineSegment(sketch, "E75.2.1", {"start": v(5.06, 2.37) * mm, "end": v(8.25, 5.54) * mm});
            skLineSegment(sketch, "E75.2.2", {"start": v(8.24, -0.82) * mm, "end": v(5.06, 2.37) * mm});
            skLineSegment(sketch, "E75.2.3", {"start": v(11.42, 2.35) * mm, "end": v(8.24, -0.82) * mm});
            skLineSegment(sketch, "E75.3.0", {"start": v(-8.82, 2.3) * mm, "end": v(-5.63, 5.48) * mm});
            skLineSegment(sketch, "E75.3.1", {"start": v(-5.65, -0.88) * mm, "end": v(-8.82, 2.3) * mm});
            skLineSegment(sketch, "E75.3.2", {"start": v(-2.46, 2.29) * mm, "end": v(-5.65, -0.88) * mm});
            skLineSegment(sketch, "E75.3.3", {"start": v(-5.63, 5.48) * mm, "end": v(-2.46, 2.29) * mm});
            skPoint(sketch, "E75.center", {"position": v(1.33, -4.61) * mm});
            skCircle(sketch, "E76.0", {"center": v(-5.57, -11.58) * mm, "radius": 2.53 * mm});
            skCircle(sketch, "E77.1.0", {"center": v(8.3, -11.52) * mm, "radius": 2.53 * mm});
            skCircle(sketch, "E77.2.0", {"center": v(8.24, 2.36) * mm, "radius": 2.53 * mm});
            skCircle(sketch, "E77.3.0", {"center": v(-5.64, 2.3) * mm, "radius": 2.53 * mm});
            skSolve(sketch);
        }
        {
            var Q0;
            {var subQ0=sQuery(id+"F34.wireOp",EDGE,"E77.1.0");var subQ1=sQuery(id+"F34.wireOp",EDGE,"E75.1.0");var subQ2=makeQuery(id+"F34.imprint","INTERSECT",VERTEX,{"disambiguationData":[OD(0.0)],"derivedFrom":[subQ1,subQ0]});Q0=makeQuery(id+"F34.imprint","IMPRINT",FACE,{"disambiguationData":[TD([[makeQuery(id+"F34.imprint","IMPRINT",EDGE,{"disambiguationData":[TD([[subQ2,-1.0]])],"derivedFrom":subQ1}),1.0]])]});}
            var Q1;
            {var subQ0=sQuery(id+"F34.wireOp",EDGE,"E77.1.0");var subQ1=sQuery(id+"F34.wireOp",EDGE,"E75.1.3");var subQ2=makeQuery(id+"F34.imprint","INTERSECT",VERTEX,{"disambiguationData":[OD(0.0)],"derivedFrom":[subQ1,subQ0]});Q1=makeQuery(id+"F34.imprint","IMPRINT",FACE,{"disambiguationData":[TD([[makeQuery(id+"F34.imprint","IMPRINT",EDGE,{"disambiguationData":[TD([[subQ2,-1.0]])],"derivedFrom":subQ1}),1.0]])]});}
            var Q2;
            {var subQ0=sQuery(id+"F34.wireOp",EDGE,"E77.1.0");var subQ1=sQuery(id+"F34.wireOp",EDGE,"E75.1.1");var subQ2=makeQuery(id+"F34.imprint","INTERSECT",VERTEX,{"disambiguationData":[OD(0.0)],"derivedFrom":[subQ1,subQ0]});Q2=makeQuery(id+"F34.imprint","IMPRINT",FACE,{"disambiguationData":[TD([[makeQuery(id+"F34.imprint","IMPRINT",EDGE,{"disambiguationData":[TD([[subQ2,-1.0]])],"derivedFrom":subQ1}),1.0]])]});}
            var Q3;
            {var subQ0=sQuery(id+"F34.wireOp",EDGE,"E77.1.0");var subQ1=sQuery(id+"F34.wireOp",EDGE,"E75.1.2");var subQ2=makeQuery(id+"F34.imprint","INTERSECT",VERTEX,{"disambiguationData":[OD(0.0)],"derivedFrom":[subQ1,subQ0]});Q3=makeQuery(id+"F34.imprint","IMPRINT",FACE,{"disambiguationData":[TD([[makeQuery(id+"F34.imprint","IMPRINT",EDGE,{"disambiguationData":[TD([[subQ2,-1.0]])],"derivedFrom":subQ1}),1.0]])]});}
            var Q4;
            {var subQ0=sQuery(id+"F34.wireOp",EDGE,"E70");var subQ1=makeQuery(id+"F34.imprint","INTERSECT",VERTEX,{"derivedFrom":[subQ0,sQuery(id+"F34.wireOp",EDGE,"E73")]});Q4=makeQuery(id+"F34.imprint","IMPRINT",FACE,{"disambiguationData":[TD([[makeQuery(id+"F34.imprint","IMPRINT",EDGE,{"disambiguationData":[TD([[subQ1,1.0]])],"derivedFrom":subQ0}),1.0]])]});}
            var Q5;
            {var subQ0=sQuery(id+"F34.wireOp",EDGE,"E76.0");var subQ1=sQuery(id+"F34.wireOp",EDGE,"E71");var subQ2=makeQuery(id+"F34.imprint","INTERSECT",VERTEX,{"disambiguationData":[OD(0.0)],"derivedFrom":[subQ1,subQ0]});Q5=makeQuery(id+"F34.imprint","IMPRINT",FACE,{"disambiguationData":[TD([[makeQuery(id+"F34.imprint","IMPRINT",EDGE,{"disambiguationData":[TD([[subQ2,-1.0]])],"derivedFrom":subQ1}),1.0]])]});}
            var Q6;
            {var subQ0=sQuery(id+"F34.wireOp",EDGE,"E72");var subQ1=makeQuery(id+"F34.imprint","INTERSECT",VERTEX,{"derivedFrom":[subQ0,sQuery(id+"F34.wireOp",EDGE,"E73")]});Q6=makeQuery(id+"F34.imprint","IMPRINT",FACE,{"disambiguationData":[TD([[makeQuery(id+"F34.imprint","IMPRINT",EDGE,{"disambiguationData":[TD([[subQ1,1.0]])],"derivedFrom":subQ0}),1.0]])]});}
            var Q7;
            {var subQ0=sQuery(id+"F34.wireOp",EDGE,"E76.0");var subQ1=sQuery(id+"F34.wireOp",EDGE,"E69");var subQ2=makeQuery(id+"F34.imprint","INTERSECT",VERTEX,{"disambiguationData":[OD(0.0)],"derivedFrom":[subQ1,subQ0]});Q7=makeQuery(id+"F34.imprint","IMPRINT",FACE,{"disambiguationData":[TD([[makeQuery(id+"F34.imprint","IMPRINT",EDGE,{"disambiguationData":[TD([[subQ2,-1.0]])],"derivedFrom":subQ1}),1.0]])]});}
            var Q8;
            {var subQ0=sQuery(id+"F34.wireOp",EDGE,"E77.3.0");var subQ1=sQuery(id+"F34.wireOp",EDGE,"E75.3.0");var subQ2=makeQuery(id+"F34.imprint","INTERSECT",VERTEX,{"disambiguationData":[OD(0.0)],"derivedFrom":[subQ1,subQ0]});Q8=makeQuery(id+"F34.imprint","IMPRINT",FACE,{"disambiguationData":[TD([[makeQuery(id+"F34.imprint","IMPRINT",EDGE,{"disambiguationData":[TD([[subQ2,-1.0]])],"derivedFrom":subQ1}),1.0]])]});}
            var Q9;
            {var subQ0=sQuery(id+"F34.wireOp",EDGE,"E77.3.0");var subQ1=sQuery(id+"F34.wireOp",EDGE,"E75.3.3");var subQ2=makeQuery(id+"F34.imprint","INTERSECT",VERTEX,{"disambiguationData":[OD(0.0)],"derivedFrom":[subQ1,subQ0]});Q9=makeQuery(id+"F34.imprint","IMPRINT",FACE,{"disambiguationData":[TD([[makeQuery(id+"F34.imprint","IMPRINT",EDGE,{"disambiguationData":[TD([[subQ2,-1.0]])],"derivedFrom":subQ1}),1.0]])]});}
            var Q10;
            {var subQ0=sQuery(id+"F34.wireOp",EDGE,"E77.3.0");var subQ1=sQuery(id+"F34.wireOp",EDGE,"E75.3.1");var subQ2=makeQuery(id+"F34.imprint","INTERSECT",VERTEX,{"disambiguationData":[OD(0.0)],"derivedFrom":[subQ1,subQ0]});Q10=makeQuery(id+"F34.imprint","IMPRINT",FACE,{"disambiguationData":[TD([[makeQuery(id+"F34.imprint","IMPRINT",EDGE,{"disambiguationData":[TD([[subQ2,-1.0]])],"derivedFrom":subQ1}),1.0]])]});}
            var Q11;
            {var subQ0=sQuery(id+"F34.wireOp",EDGE,"E77.3.0");var subQ1=sQuery(id+"F34.wireOp",EDGE,"E75.3.2");var subQ2=makeQuery(id+"F34.imprint","INTERSECT",VERTEX,{"disambiguationData":[OD(0.0)],"derivedFrom":[subQ1,subQ0]});Q11=makeQuery(id+"F34.imprint","IMPRINT",FACE,{"disambiguationData":[TD([[makeQuery(id+"F34.imprint","IMPRINT",EDGE,{"disambiguationData":[TD([[subQ2,-1.0]])],"derivedFrom":subQ1}),1.0]])]});}
            var Q12;
            {var subQ0=sQuery(id+"F34.wireOp",EDGE,"E77.2.0");var subQ1=sQuery(id+"F34.wireOp",EDGE,"E75.2.0");var subQ2=makeQuery(id+"F34.imprint","INTERSECT",VERTEX,{"disambiguationData":[OD(0.0)],"derivedFrom":[subQ1,subQ0]});Q12=makeQuery(id+"F34.imprint","IMPRINT",FACE,{"disambiguationData":[TD([[makeQuery(id+"F34.imprint","IMPRINT",EDGE,{"disambiguationData":[TD([[subQ2,-1.0]])],"derivedFrom":subQ1}),1.0]])]});}
            var Q13;
            {var subQ0=sQuery(id+"F34.wireOp",EDGE,"E77.2.0");var subQ1=sQuery(id+"F34.wireOp",EDGE,"E75.2.1");var subQ2=makeQuery(id+"F34.imprint","INTERSECT",VERTEX,{"disambiguationData":[OD(0.0)],"derivedFrom":[subQ1,subQ0]});Q13=makeQuery(id+"F34.imprint","IMPRINT",FACE,{"disambiguationData":[TD([[makeQuery(id+"F34.imprint","IMPRINT",EDGE,{"disambiguationData":[TD([[subQ2,-1.0]])],"derivedFrom":subQ1}),1.0]])]});}
            var Q14;
            {var subQ0=sQuery(id+"F34.wireOp",EDGE,"E77.2.0");var subQ1=sQuery(id+"F34.wireOp",EDGE,"E75.2.2");var subQ2=makeQuery(id+"F34.imprint","INTERSECT",VERTEX,{"disambiguationData":[OD(0.0)],"derivedFrom":[subQ1,subQ0]});Q14=makeQuery(id+"F34.imprint","IMPRINT",FACE,{"disambiguationData":[TD([[makeQuery(id+"F34.imprint","IMPRINT",EDGE,{"disambiguationData":[TD([[subQ2,-1.0]])],"derivedFrom":subQ1}),1.0]])]});}
            var Q15;
            {var subQ0=sQuery(id+"F34.wireOp",EDGE,"E77.2.0");var subQ1=sQuery(id+"F34.wireOp",EDGE,"E75.2.3");var subQ2=makeQuery(id+"F34.imprint","INTERSECT",VERTEX,{"disambiguationData":[OD(0.0)],"derivedFrom":[subQ1,subQ0]});Q15=makeQuery(id+"F34.imprint","IMPRINT",FACE,{"disambiguationData":[TD([[makeQuery(id+"F34.imprint","IMPRINT",EDGE,{"disambiguationData":[TD([[subQ2,-1.0]])],"derivedFrom":subQ1}),1.0]])]});}
            extrude(context, id + "F35", {"entities" : qUnion([Q0, Q1, Q2, Q3, Q4, Q5, Q6, Q7, Q8, Q9, Q10, Q11, Q12, Q13, Q14, Q15]), "operationType" : NewBodyOperationType.ADD, "oppositeDirection" : true, "depth" : 13.8 * mm, "offsetDistance" : 25.4 * mm});
        }
        {
            var Q0;
            {var subQ0=sQuery(id+"F34.wireOp",EDGE,"E77.3.0");var subQ1=sQuery(id+"F34.wireOp",EDGE,"E77.2.0");var subQ2=sQuery(id+"F34.wireOp",EDGE,"E77.1.0");var subQ3=sQuery(id+"F34.wireOp",EDGE,"E76.0");Q0=makeQuery(id+"F35.boolean.opBoolean","MERGE",FACE,{"derivedFrom":[makeQuery(id+"F9.boolean.opBoolean","MERGE",FACE,{"derivedFrom":[makeQuery(id+"F1.opExtrude","CAP_FACE",FACE,{"disambiguationData":[OSD([sQuery(id+"F0.wireOp",EDGE,"E0.bottom"),sQuery(id+"F0.wireOp",EDGE,"E0.top"),sQuery(id+"F0.wireOp",EDGE,"E0.left"),sQuery(id+"F0.wireOp",EDGE,"E0.right")])],"isStart":false}),makeQuery(id+"F9.opExtrude","CAP_FACE",FACE,{"disambiguationData":[OSD([sQuery(id+"F8.wireOp",EDGE,"E8")])],"isStart":false})]}),makeQuery(id+"F35.opExtrude","CAP_FACE",FACE,{"disambiguationData":[OSD([sQuery(id+"F34.wireOp",EDGE,"E69"),subQ3])],"isStart":true}),makeQuery(id+"F35.opExtrude","CAP_FACE",FACE,{"disambiguationData":[OSD([sQuery(id+"F34.wireOp",EDGE,"E70"),subQ3])],"isStart":true}),makeQuery(id+"F35.opExtrude","CAP_FACE",FACE,{"disambiguationData":[OSD([sQuery(id+"F34.wireOp",EDGE,"E71"),subQ3])],"isStart":true}),makeQuery(id+"F35.opExtrude","CAP_FACE",FACE,{"disambiguationData":[OSD([sQuery(id+"F34.wireOp",EDGE,"E72"),subQ3])],"isStart":true}),makeQuery(id+"F35.opExtrude","CAP_FACE",FACE,{"disambiguationData":[OSD([sQuery(id+"F34.wireOp",EDGE,"E75.1.0"),subQ2])],"isStart":true}),makeQuery(id+"F35.opExtrude","CAP_FACE",FACE,{"disambiguationData":[OSD([sQuery(id+"F34.wireOp",EDGE,"E75.1.1"),subQ2])],"isStart":true}),makeQuery(id+"F35.opExtrude","CAP_FACE",FACE,{"disambiguationData":[OSD([sQuery(id+"F34.wireOp",EDGE,"E75.1.2"),subQ2])],"isStart":true}),makeQuery(id+"F35.opExtrude","CAP_FACE",FACE,{"disambiguationData":[OSD([sQuery(id+"F34.wireOp",EDGE,"E75.1.3"),subQ2])],"isStart":true}),makeQuery(id+"F35.opExtrude","CAP_FACE",FACE,{"disambiguationData":[OSD([sQuery(id+"F34.wireOp",EDGE,"E75.2.0"),subQ1])],"isStart":true}),makeQuery(id+"F35.opExtrude","CAP_FACE",FACE,{"disambiguationData":[OSD([sQuery(id+"F34.wireOp",EDGE,"E75.2.1"),subQ1])],"isStart":true}),makeQuery(id+"F35.opExtrude","CAP_FACE",FACE,{"disambiguationData":[OSD([sQuery(id+"F34.wireOp",EDGE,"E75.2.2"),subQ1])],"isStart":true}),makeQuery(id+"F35.opExtrude","CAP_FACE",FACE,{"disambiguationData":[OSD([sQuery(id+"F34.wireOp",EDGE,"E75.2.3"),subQ1])],"isStart":true}),makeQuery(id+"F35.opExtrude","CAP_FACE",FACE,{"disambiguationData":[OSD([sQuery(id+"F34.wireOp",EDGE,"E75.3.0"),subQ0])],"isStart":true}),makeQuery(id+"F35.opExtrude","CAP_FACE",FACE,{"disambiguationData":[OSD([sQuery(id+"F34.wireOp",EDGE,"E75.3.1"),subQ0])],"isStart":true}),makeQuery(id+"F35.opExtrude","CAP_FACE",FACE,{"disambiguationData":[OSD([sQuery(id+"F34.wireOp",EDGE,"E75.3.2"),subQ0])],"isStart":true}),makeQuery(id+"F35.opExtrude","CAP_FACE",FACE,{"disambiguationData":[OSD([sQuery(id+"F34.wireOp",EDGE,"E75.3.3"),subQ0])],"isStart":true})]});}
            var sketch = newSketch(context, id + "F36", { "sketchPlane" : qUnion([Q0])});
            skCircle(sketch, "E78", {"center": v(8.24, 2.36) * mm, "radius": 2.53 * mm});
            skLineSegment(sketch, "E79.0", {"start": v(10.65, 1.58) * mm, "end": v(9.01, -0.05) * mm});
            skLineSegment(sketch, "E79.1", {"start": v(9.02, 4.76) * mm, "end": v(10.65, 3.13) * mm});
            skLineSegment(sketch, "E79.2", {"start": v(5.84, 3.14) * mm, "end": v(7.48, 4.77) * mm});
            skLineSegment(sketch, "E79.3", {"start": v(7.46, -0.04) * mm, "end": v(5.84, 1.6) * mm});
            skCircle(sketch, "E80.1.0", {"center": v(-5.64, 2.3) * mm, "radius": 2.53 * mm});
            skLineSegment(sketch, "E80.1.1", {"start": v(-4.86, 4.7) * mm, "end": v(-3.23, 3.06) * mm});
            skLineSegment(sketch, "E80.1.2", {"start": v(-8.04, 3.07) * mm, "end": v(-6.4, 4.7) * mm});
            skLineSegment(sketch, "E80.1.3", {"start": v(-6.42, -0.1) * mm, "end": v(-8.05, 1.53) * mm});
            skLineSegment(sketch, "E80.1.4", {"start": v(-3.23, 1.52) * mm, "end": v(-4.87, -0.11) * mm});
            skCircle(sketch, "E80.2.0", {"center": v(-5.57, -11.58) * mm, "radius": 2.53 * mm});
            skLineSegment(sketch, "E80.2.1", {"start": v(-7.98, -10.8) * mm, "end": v(-6.34, -9.18) * mm});
            skLineSegment(sketch, "E80.2.2", {"start": v(-6.35, -13.99) * mm, "end": v(-7.98, -12.35) * mm});
            skLineSegment(sketch, "E80.2.3", {"start": v(-3.17, -12.36) * mm, "end": v(-4.8, -14) * mm});
            skLineSegment(sketch, "E80.2.4", {"start": v(-4.8, -9.18) * mm, "end": v(-3.17, -10.82) * mm});
            skCircle(sketch, "E80.3.0", {"center": v(8.3, -11.52) * mm, "radius": 2.53 * mm});
            skLineSegment(sketch, "E80.3.1", {"start": v(7.53, -13.93) * mm, "end": v(5.9, -12.29) * mm});
            skLineSegment(sketch, "E80.3.2", {"start": v(10.71, -12.3) * mm, "end": v(9.07, -13.93) * mm});
            skLineSegment(sketch, "E80.3.3", {"start": v(9.08, -9.12) * mm, "end": v(10.71, -10.75) * mm});
            skLineSegment(sketch, "E80.3.4", {"start": v(5.9, -10.74) * mm, "end": v(7.54, -9.11) * mm});
            skPoint(sketch, "E80.center", {"position": v(1.33, -4.61) * mm});
            skSolve(sketch);
        }
        {
            var Q0;
            {var subQ0=sQuery(id+"F36.wireOp",EDGE,"E79.1");var subQ1=sQuery(id+"F36.wireOp",EDGE,"E78");var subQ2=makeQuery(id+"F36.imprint","INTERSECT",VERTEX,{"disambiguationData":[OD(0.0)],"derivedFrom":[subQ1,subQ0]});Q0=makeQuery(id+"F36.imprint","IMPRINT",FACE,{"disambiguationData":[TD([[makeQuery(id+"F36.imprint","IMPRINT",EDGE,{"disambiguationData":[TD([[subQ2,1.0]])],"derivedFrom":subQ1}),1.0]])]});}
            var Q1;
            {var subQ0=sQuery(id+"F36.wireOp",EDGE,"E79.2");var subQ1=sQuery(id+"F36.wireOp",EDGE,"E78");var subQ2=makeQuery(id+"F36.imprint","INTERSECT",VERTEX,{"disambiguationData":[OD(0.0)],"derivedFrom":[subQ1,subQ0]});Q1=makeQuery(id+"F36.imprint","IMPRINT",FACE,{"disambiguationData":[TD([[makeQuery(id+"F36.imprint","IMPRINT",EDGE,{"disambiguationData":[TD([[subQ2,-1.0]])],"derivedFrom":subQ1}),1.0]])]});}
            var Q2;
            {var subQ0=sQuery(id+"F36.wireOp",EDGE,"E79.3");var subQ1=sQuery(id+"F36.wireOp",EDGE,"E78");var subQ2=makeQuery(id+"F36.imprint","INTERSECT",VERTEX,{"disambiguationData":[OD(0.0)],"derivedFrom":[subQ1,subQ0]});Q2=makeQuery(id+"F36.imprint","IMPRINT",FACE,{"disambiguationData":[TD([[makeQuery(id+"F36.imprint","IMPRINT",EDGE,{"disambiguationData":[TD([[subQ2,-1.0]])],"derivedFrom":subQ1}),1.0]])]});}
            var Q3;
            {var subQ0=sQuery(id+"F36.wireOp",EDGE,"E79.0");var subQ1=sQuery(id+"F36.wireOp",EDGE,"E78");var subQ2=makeQuery(id+"F36.imprint","INTERSECT",VERTEX,{"disambiguationData":[OD(0.0)],"derivedFrom":[subQ1,subQ0]});Q3=makeQuery(id+"F36.imprint","IMPRINT",FACE,{"disambiguationData":[TD([[makeQuery(id+"F36.imprint","IMPRINT",EDGE,{"disambiguationData":[TD([[subQ2,-1.0]])],"derivedFrom":subQ1}),1.0]])]});}
            var Q4;
            {var subQ0=sQuery(id+"F36.wireOp",EDGE,"E80.1.2");var subQ1=sQuery(id+"F36.wireOp",EDGE,"E80.1.0");var subQ2=makeQuery(id+"F36.imprint","INTERSECT",VERTEX,{"disambiguationData":[OD(0.0)],"derivedFrom":[subQ1,subQ0]});Q4=makeQuery(id+"F36.imprint","IMPRINT",FACE,{"disambiguationData":[TD([[makeQuery(id+"F36.imprint","IMPRINT",EDGE,{"disambiguationData":[TD([[subQ2,1.0]])],"derivedFrom":subQ1}),1.0]])]});}
            var Q5;
            {var subQ0=sQuery(id+"F36.wireOp",EDGE,"E80.1.3");var subQ1=sQuery(id+"F36.wireOp",EDGE,"E80.1.0");var subQ2=makeQuery(id+"F36.imprint","INTERSECT",VERTEX,{"disambiguationData":[OD(0.0)],"derivedFrom":[subQ1,subQ0]});Q5=makeQuery(id+"F36.imprint","IMPRINT",FACE,{"disambiguationData":[TD([[makeQuery(id+"F36.imprint","IMPRINT",EDGE,{"disambiguationData":[TD([[subQ2,-1.0]])],"derivedFrom":subQ1}),1.0]])]});}
            var Q6;
            {var subQ0=sQuery(id+"F36.wireOp",EDGE,"E80.1.4");var subQ1=sQuery(id+"F36.wireOp",EDGE,"E80.1.0");var subQ2=makeQuery(id+"F36.imprint","INTERSECT",VERTEX,{"disambiguationData":[OD(0.0)],"derivedFrom":[subQ1,subQ0]});Q6=makeQuery(id+"F36.imprint","IMPRINT",FACE,{"disambiguationData":[TD([[makeQuery(id+"F36.imprint","IMPRINT",EDGE,{"disambiguationData":[TD([[subQ2,-1.0]])],"derivedFrom":subQ1}),1.0]])]});}
            var Q7;
            {var subQ0=sQuery(id+"F36.wireOp",EDGE,"E80.1.1");var subQ1=sQuery(id+"F36.wireOp",EDGE,"E80.1.0");var subQ2=makeQuery(id+"F36.imprint","INTERSECT",VERTEX,{"disambiguationData":[OD(0.0)],"derivedFrom":[subQ1,subQ0]});Q7=makeQuery(id+"F36.imprint","IMPRINT",FACE,{"disambiguationData":[TD([[makeQuery(id+"F36.imprint","IMPRINT",EDGE,{"disambiguationData":[TD([[subQ2,-1.0]])],"derivedFrom":subQ1}),1.0]])]});}
            var Q8;
            {var subQ0=sQuery(id+"F36.wireOp",EDGE,"E80.2.2");var subQ1=sQuery(id+"F36.wireOp",EDGE,"E80.2.0");var subQ2=makeQuery(id+"F36.imprint","INTERSECT",VERTEX,{"disambiguationData":[OD(0.0)],"derivedFrom":[subQ1,subQ0]});Q8=makeQuery(id+"F36.imprint","IMPRINT",FACE,{"disambiguationData":[TD([[makeQuery(id+"F36.imprint","IMPRINT",EDGE,{"disambiguationData":[TD([[subQ2,1.0]])],"derivedFrom":subQ1}),1.0]])]});}
            var Q9;
            {var subQ0=sQuery(id+"F36.wireOp",EDGE,"E80.2.3");var subQ1=sQuery(id+"F36.wireOp",EDGE,"E80.2.0");var subQ2=makeQuery(id+"F36.imprint","INTERSECT",VERTEX,{"disambiguationData":[OD(0.0)],"derivedFrom":[subQ1,subQ0]});Q9=makeQuery(id+"F36.imprint","IMPRINT",FACE,{"disambiguationData":[TD([[makeQuery(id+"F36.imprint","IMPRINT",EDGE,{"disambiguationData":[TD([[subQ2,-1.0]])],"derivedFrom":subQ1}),1.0]])]});}
            var Q10;
            {var subQ0=sQuery(id+"F36.wireOp",EDGE,"E80.2.4");var subQ1=sQuery(id+"F36.wireOp",EDGE,"E80.2.0");var subQ2=makeQuery(id+"F36.imprint","INTERSECT",VERTEX,{"disambiguationData":[OD(0.0)],"derivedFrom":[subQ1,subQ0]});Q10=makeQuery(id+"F36.imprint","IMPRINT",FACE,{"disambiguationData":[TD([[makeQuery(id+"F36.imprint","IMPRINT",EDGE,{"disambiguationData":[TD([[subQ2,-1.0]])],"derivedFrom":subQ1}),1.0]])]});}
            var Q11;
            {var subQ0=sQuery(id+"F36.wireOp",EDGE,"E80.2.1");var subQ1=sQuery(id+"F36.wireOp",EDGE,"E80.2.0");var subQ2=makeQuery(id+"F36.imprint","INTERSECT",VERTEX,{"disambiguationData":[OD(0.0)],"derivedFrom":[subQ1,subQ0]});Q11=makeQuery(id+"F36.imprint","IMPRINT",FACE,{"disambiguationData":[TD([[makeQuery(id+"F36.imprint","IMPRINT",EDGE,{"disambiguationData":[TD([[subQ2,-1.0]])],"derivedFrom":subQ1}),1.0]])]});}
            var Q12;
            {var subQ0=sQuery(id+"F36.wireOp",EDGE,"E80.3.2");var subQ1=sQuery(id+"F36.wireOp",EDGE,"E80.3.0");var subQ2=makeQuery(id+"F36.imprint","INTERSECT",VERTEX,{"disambiguationData":[OD(0.0)],"derivedFrom":[subQ1,subQ0]});Q12=makeQuery(id+"F36.imprint","IMPRINT",FACE,{"disambiguationData":[TD([[makeQuery(id+"F36.imprint","IMPRINT",EDGE,{"disambiguationData":[TD([[subQ2,1.0]])],"derivedFrom":subQ1}),1.0]])]});}
            var Q13;
            {var subQ0=sQuery(id+"F36.wireOp",EDGE,"E80.3.3");var subQ1=sQuery(id+"F36.wireOp",EDGE,"E80.3.0");var subQ2=makeQuery(id+"F36.imprint","INTERSECT",VERTEX,{"disambiguationData":[OD(0.0)],"derivedFrom":[subQ1,subQ0]});Q13=makeQuery(id+"F36.imprint","IMPRINT",FACE,{"disambiguationData":[TD([[makeQuery(id+"F36.imprint","IMPRINT",EDGE,{"disambiguationData":[TD([[subQ2,-1.0]])],"derivedFrom":subQ1}),1.0]])]});}
            var Q14;
            {var subQ0=sQuery(id+"F36.wireOp",EDGE,"E80.3.4");var subQ1=sQuery(id+"F36.wireOp",EDGE,"E80.3.0");var subQ2=makeQuery(id+"F36.imprint","INTERSECT",VERTEX,{"disambiguationData":[OD(0.0)],"derivedFrom":[subQ1,subQ0]});Q14=makeQuery(id+"F36.imprint","IMPRINT",FACE,{"disambiguationData":[TD([[makeQuery(id+"F36.imprint","IMPRINT",EDGE,{"disambiguationData":[TD([[subQ2,-1.0]])],"derivedFrom":subQ1}),1.0]])]});}
            var Q15;
            {var subQ0=sQuery(id+"F36.wireOp",EDGE,"E80.3.1");var subQ1=sQuery(id+"F36.wireOp",EDGE,"E80.3.0");var subQ2=makeQuery(id+"F36.imprint","INTERSECT",VERTEX,{"disambiguationData":[OD(0.0)],"derivedFrom":[subQ1,subQ0]});Q15=makeQuery(id+"F36.imprint","IMPRINT",FACE,{"disambiguationData":[TD([[makeQuery(id+"F36.imprint","IMPRINT",EDGE,{"disambiguationData":[TD([[subQ2,-1.0]])],"derivedFrom":subQ1}),1.0]])]});}
            extrude(context, id + "F37", {"entities" : qUnion([Q0, Q1, Q2, Q3, Q4, Q5, Q6, Q7, Q8, Q9, Q10, Q11, Q12, Q13, Q14, Q15]), "operationType" : NewBodyOperationType.REMOVE, "oppositeDirection" : true, "depth" : 0.38 * mm, "offsetDistance" : 25.4 * mm});
        }
        {
            var Q0;
            {var subQ0=sQuery(id+"F34.wireOp",EDGE,"E77.3.0");var subQ1=sQuery(id+"F34.wireOp",EDGE,"E77.2.0");var subQ2=sQuery(id+"F34.wireOp",EDGE,"E77.1.0");var subQ3=sQuery(id+"F34.wireOp",EDGE,"E76.0");Q0=makeQuery(id+"F35.boolean.opBoolean","MERGE",FACE,{"derivedFrom":[makeQuery(id+"F7.boolean.opBoolean","MERGE",FACE,{"derivedFrom":[makeQuery(id+"F1.opExtrude","CAP_FACE",FACE,{"disambiguationData":[OSD([sQuery(id+"F0.wireOp",EDGE,"E0.bottom"),sQuery(id+"F0.wireOp",EDGE,"E0.top"),sQuery(id+"F0.wireOp",EDGE,"E0.left"),sQuery(id+"F0.wireOp",EDGE,"E0.right")])],"isStart":true}),makeQuery(id+"F7.opExtrude","CAP_FACE",FACE,{"disambiguationData":[OSD([sQuery(id+"F6.wireOp",EDGE,"E5")])],"isStart":false})]}),makeQuery(id+"F35.opExtrude","CAP_FACE",FACE,{"disambiguationData":[OSD([sQuery(id+"F34.wireOp",EDGE,"E69"),subQ3])],"isStart":false}),makeQuery(id+"F35.opExtrude","CAP_FACE",FACE,{"disambiguationData":[OSD([sQuery(id+"F34.wireOp",EDGE,"E70"),subQ3])],"isStart":false}),makeQuery(id+"F35.opExtrude","CAP_FACE",FACE,{"disambiguationData":[OSD([sQuery(id+"F34.wireOp",EDGE,"E71"),subQ3])],"isStart":false}),makeQuery(id+"F35.opExtrude","CAP_FACE",FACE,{"disambiguationData":[OSD([sQuery(id+"F34.wireOp",EDGE,"E72"),subQ3])],"isStart":false}),makeQuery(id+"F35.opExtrude","CAP_FACE",FACE,{"disambiguationData":[OSD([sQuery(id+"F34.wireOp",EDGE,"E75.1.0"),subQ2])],"isStart":false}),makeQuery(id+"F35.opExtrude","CAP_FACE",FACE,{"disambiguationData":[OSD([sQuery(id+"F34.wireOp",EDGE,"E75.1.1"),subQ2])],"isStart":false}),makeQuery(id+"F35.opExtrude","CAP_FACE",FACE,{"disambiguationData":[OSD([sQuery(id+"F34.wireOp",EDGE,"E75.1.2"),subQ2])],"isStart":false}),makeQuery(id+"F35.opExtrude","CAP_FACE",FACE,{"disambiguationData":[OSD([sQuery(id+"F34.wireOp",EDGE,"E75.1.3"),subQ2])],"isStart":false}),makeQuery(id+"F35.opExtrude","CAP_FACE",FACE,{"disambiguationData":[OSD([sQuery(id+"F34.wireOp",EDGE,"E75.2.0"),subQ1])],"isStart":false}),makeQuery(id+"F35.opExtrude","CAP_FACE",FACE,{"disambiguationData":[OSD([sQuery(id+"F34.wireOp",EDGE,"E75.2.1"),subQ1])],"isStart":false}),makeQuery(id+"F35.opExtrude","CAP_FACE",FACE,{"disambiguationData":[OSD([sQuery(id+"F34.wireOp",EDGE,"E75.2.2"),subQ1])],"isStart":false}),makeQuery(id+"F35.opExtrude","CAP_FACE",FACE,{"disambiguationData":[OSD([sQuery(id+"F34.wireOp",EDGE,"E75.2.3"),subQ1])],"isStart":false}),makeQuery(id+"F35.opExtrude","CAP_FACE",FACE,{"disambiguationData":[OSD([sQuery(id+"F34.wireOp",EDGE,"E75.3.0"),subQ0])],"isStart":false}),makeQuery(id+"F35.opExtrude","CAP_FACE",FACE,{"disambiguationData":[OSD([sQuery(id+"F34.wireOp",EDGE,"E75.3.1"),subQ0])],"isStart":false}),makeQuery(id+"F35.opExtrude","CAP_FACE",FACE,{"disambiguationData":[OSD([sQuery(id+"F34.wireOp",EDGE,"E75.3.2"),subQ0])],"isStart":false}),makeQuery(id+"F35.opExtrude","CAP_FACE",FACE,{"disambiguationData":[OSD([sQuery(id+"F34.wireOp",EDGE,"E75.3.3"),subQ0])],"isStart":false})]});}
            var sketch = newSketch(context, id + "F38", { "sketchPlane" : qUnion([Q0])});
            skCircle(sketch, "E81", {"center": v(8.24, -2.36) * mm, "radius": 2.53 * mm});
            skLineSegment(sketch, "E82.0", {"start": v(5.84, -3.14) * mm, "end": v(7.48, -4.77) * mm});
            skLineSegment(sketch, "E82.1", {"start": v(9.02, -4.76) * mm, "end": v(10.65, -3.13) * mm});
            skLineSegment(sketch, "E82.3", {"start": v(10.65, -1.58) * mm, "end": v(9.01, 0.05) * mm});
            skLineSegment(sketch, "E82.4", {"start": v(7.46, 0.04) * mm, "end": v(5.84, -1.6) * mm});
            skCircle(sketch, "E83.1.0", {"center": v(8.3, 11.52) * mm, "radius": 2.53 * mm});
            skLineSegment(sketch, "E83.1.1", {"start": v(5.9, 10.74) * mm, "end": v(7.54, 9.11) * mm});
            skLineSegment(sketch, "E83.1.2", {"start": v(9.08, 9.12) * mm, "end": v(10.71, 10.75) * mm});
            skLineSegment(sketch, "E83.1.3", {"start": v(10.71, 12.3) * mm, "end": v(9.07, 13.93) * mm});
            skLineSegment(sketch, "E83.1.4", {"start": v(7.53, 13.93) * mm, "end": v(5.9, 12.29) * mm});
            skCircle(sketch, "E83.2.0", {"center": v(-5.57, 11.58) * mm, "radius": 2.53 * mm});
            skLineSegment(sketch, "E83.2.1", {"start": v(-4.8, 9.18) * mm, "end": v(-3.17, 10.82) * mm});
            skLineSegment(sketch, "E83.2.2", {"start": v(-3.17, 12.36) * mm, "end": v(-4.8, 14) * mm});
            skLineSegment(sketch, "E83.2.3", {"start": v(-6.35, 13.99) * mm, "end": v(-7.98, 12.35) * mm});
            skLineSegment(sketch, "E83.2.4", {"start": v(-7.98, 10.8) * mm, "end": v(-6.34, 9.18) * mm});
            skCircle(sketch, "E83.3.0", {"center": v(-5.64, -2.3) * mm, "radius": 2.53 * mm});
            skLineSegment(sketch, "E83.3.1", {"start": v(-3.23, -1.52) * mm, "end": v(-4.87, 0.11) * mm});
            skLineSegment(sketch, "E83.3.2", {"start": v(-6.42, 0.1) * mm, "end": v(-8.05, -1.53) * mm});
            skLineSegment(sketch, "E83.3.3", {"start": v(-8.04, -3.07) * mm, "end": v(-6.4, -4.7) * mm});
            skLineSegment(sketch, "E83.3.4", {"start": v(-4.86, -4.7) * mm, "end": v(-3.23, -3.06) * mm});
            skPoint(sketch, "E83.center", {"position": v(1.33, 4.61) * mm});
            skSolve(sketch);
        }
        {
            var Q0;
            {var subQ0=sQuery(id+"F38.wireOp",EDGE,"E82.3");Q0=makeQuery(id+"F38.imprint","IMPRINT",FACE,{"disambiguationData":[TD([[makeQuery(id+"F38.imprint","IMPRINT",EDGE,{"derivedFrom":subQ0}),-1.0]])]});}
            var Q1;
            {var subQ0=sQuery(id+"F38.wireOp",EDGE,"E82.4");Q1=makeQuery(id+"F38.imprint","IMPRINT",FACE,{"disambiguationData":[TD([[makeQuery(id+"F38.imprint","IMPRINT",EDGE,{"derivedFrom":subQ0}),-1.0]])]});}
            var Q2;
            {var subQ0=sQuery(id+"F38.wireOp",EDGE,"E82.0");Q2=makeQuery(id+"F38.imprint","IMPRINT",FACE,{"disambiguationData":[TD([[makeQuery(id+"F38.imprint","IMPRINT",EDGE,{"derivedFrom":subQ0}),-1.0]])]});}
            var Q3;
            {var subQ0=sQuery(id+"F38.wireOp",EDGE,"E82.1");Q3=makeQuery(id+"F38.imprint","IMPRINT",FACE,{"disambiguationData":[TD([[makeQuery(id+"F38.imprint","IMPRINT",EDGE,{"derivedFrom":subQ0}),-1.0]])]});}
            var Q4;
            {var subQ0=sQuery(id+"F38.wireOp",EDGE,"E83.1.4");Q4=makeQuery(id+"F38.imprint","IMPRINT",FACE,{"disambiguationData":[TD([[makeQuery(id+"F38.imprint","IMPRINT",EDGE,{"derivedFrom":subQ0}),-1.0]])]});}
            var Q5;
            {var subQ0=sQuery(id+"F38.wireOp",EDGE,"E83.1.1");Q5=makeQuery(id+"F38.imprint","IMPRINT",FACE,{"disambiguationData":[TD([[makeQuery(id+"F38.imprint","IMPRINT",EDGE,{"derivedFrom":subQ0}),-1.0]])]});}
            var Q6;
            {var subQ0=sQuery(id+"F38.wireOp",EDGE,"E83.1.2");Q6=makeQuery(id+"F38.imprint","IMPRINT",FACE,{"disambiguationData":[TD([[makeQuery(id+"F38.imprint","IMPRINT",EDGE,{"derivedFrom":subQ0}),-1.0]])]});}
            var Q7;
            {var subQ0=sQuery(id+"F38.wireOp",EDGE,"E83.1.3");Q7=makeQuery(id+"F38.imprint","IMPRINT",FACE,{"disambiguationData":[TD([[makeQuery(id+"F38.imprint","IMPRINT",EDGE,{"derivedFrom":subQ0}),-1.0]])]});}
            var Q8;
            {var subQ0=sQuery(id+"F38.wireOp",EDGE,"E83.2.4");Q8=makeQuery(id+"F38.imprint","IMPRINT",FACE,{"disambiguationData":[TD([[makeQuery(id+"F38.imprint","IMPRINT",EDGE,{"derivedFrom":subQ0}),-1.0]])]});}
            var Q9;
            {var subQ0=sQuery(id+"F38.wireOp",EDGE,"E83.2.1");Q9=makeQuery(id+"F38.imprint","IMPRINT",FACE,{"disambiguationData":[TD([[makeQuery(id+"F38.imprint","IMPRINT",EDGE,{"derivedFrom":subQ0}),-1.0]])]});}
            var Q10;
            {var subQ0=sQuery(id+"F38.wireOp",EDGE,"E83.2.2");Q10=makeQuery(id+"F38.imprint","IMPRINT",FACE,{"disambiguationData":[TD([[makeQuery(id+"F38.imprint","IMPRINT",EDGE,{"derivedFrom":subQ0}),-1.0]])]});}
            var Q11;
            {var subQ0=sQuery(id+"F38.wireOp",EDGE,"E83.2.3");Q11=makeQuery(id+"F38.imprint","IMPRINT",FACE,{"disambiguationData":[TD([[makeQuery(id+"F38.imprint","IMPRINT",EDGE,{"derivedFrom":subQ0}),-1.0]])]});}
            var Q12;
            {var subQ0=sQuery(id+"F38.wireOp",EDGE,"E83.3.4");Q12=makeQuery(id+"F38.imprint","IMPRINT",FACE,{"disambiguationData":[TD([[makeQuery(id+"F38.imprint","IMPRINT",EDGE,{"derivedFrom":subQ0}),-1.0]])]});}
            var Q13;
            {var subQ0=sQuery(id+"F38.wireOp",EDGE,"E83.3.1");Q13=makeQuery(id+"F38.imprint","IMPRINT",FACE,{"disambiguationData":[TD([[makeQuery(id+"F38.imprint","IMPRINT",EDGE,{"derivedFrom":subQ0}),-1.0]])]});}
            var Q14;
            {var subQ0=sQuery(id+"F38.wireOp",EDGE,"E83.3.2");Q14=makeQuery(id+"F38.imprint","IMPRINT",FACE,{"disambiguationData":[TD([[makeQuery(id+"F38.imprint","IMPRINT",EDGE,{"derivedFrom":subQ0}),-1.0]])]});}
            var Q15;
            {var subQ0=sQuery(id+"F38.wireOp",EDGE,"E83.3.3");Q15=makeQuery(id+"F38.imprint","IMPRINT",FACE,{"disambiguationData":[TD([[makeQuery(id+"F38.imprint","IMPRINT",EDGE,{"derivedFrom":subQ0}),-1.0]])]});}
            extrude(context, id + "F39", {"entities" : qUnion([Q0, Q1, Q2, Q3, Q4, Q5, Q6, Q7, Q8, Q9, Q10, Q11, Q12, Q13, Q14, Q15]), "operationType" : NewBodyOperationType.REMOVE, "oppositeDirection" : true, "depth" : 0.38 * mm, "offsetDistance" : 25.4 * mm});
        }
        {
            var Q0;
            Q0=makeQuery(id+"F1.opExtrude","CAP_EDGE",EDGE,{"disambiguationData":[OSD([sQuery(id+"F0.wireOp",EDGE,"E0.bottom")])],"isStart":true});
            var Q1;
            Q1=makeQuery(id+"F1.opExtrude","CAP_EDGE",EDGE,{"disambiguationData":[OSD([sQuery(id+"F0.wireOp",EDGE,"E0.left")])],"isStart":true});
            var Q2;
            Q2=makeQuery(id+"F1.opExtrude","CAP_EDGE",EDGE,{"disambiguationData":[OSD([sQuery(id+"F0.wireOp",EDGE,"E0.right")])],"isStart":true});
            var Q3;
            Q3=makeQuery(id+"F1.opExtrude","CAP_EDGE",EDGE,{"disambiguationData":[OSD([sQuery(id+"F0.wireOp",EDGE,"E0.top")])],"isStart":true});
            var Q4;
            Q4=makeQuery(id+"F1.opExtrude","CAP_EDGE",EDGE,{"disambiguationData":[OSD([sQuery(id+"F0.wireOp",EDGE,"E0.bottom")])],"isStart":false});
            var Q5;
            Q5=makeQuery(id+"F1.opExtrude","CAP_EDGE",EDGE,{"disambiguationData":[OSD([sQuery(id+"F0.wireOp",EDGE,"E0.left")])],"isStart":false});
            var Q6;
            Q6=makeQuery(id+"F1.opExtrude","CAP_EDGE",EDGE,{"disambiguationData":[OSD([sQuery(id+"F0.wireOp",EDGE,"E0.top")])],"isStart":false});
            var Q7;
            Q7=makeQuery(id+"F1.opExtrude","CAP_EDGE",EDGE,{"disambiguationData":[OSD([sQuery(id+"F0.wireOp",EDGE,"E0.right")])],"isStart":false});
            var Q8;
            Q8=makeQuery(id+"F1.opExtrude","SWEPT_EDGE",EDGE,{"disambiguationData":[OSD([sQuery(id+"F0.wireOp",EDGE,"E0.top"),sQuery(id+"F0.wireOp",EDGE,"E0.right")])]});
            var Q9;
            Q9=makeQuery(id+"F1.opExtrude","SWEPT_EDGE",EDGE,{"disambiguationData":[OSD([sQuery(id+"F0.wireOp",EDGE,"E0.bottom"),sQuery(id+"F0.wireOp",EDGE,"E0.right")])]});
            var Q10;
            Q10=makeQuery(id+"F1.opExtrude","SWEPT_EDGE",EDGE,{"disambiguationData":[OSD([sQuery(id+"F0.wireOp",EDGE,"E0.bottom"),sQuery(id+"F0.wireOp",EDGE,"E0.left")])]});
            var Q11;
            Q11=makeQuery(id+"F1.opExtrude","SWEPT_EDGE",EDGE,{"disambiguationData":[OSD([sQuery(id+"F0.wireOp",EDGE,"E0.top"),sQuery(id+"F0.wireOp",EDGE,"E0.left")])]});
            fillet(context, id + "F40", {"entities" : qUnion([Q0, Q1, Q2, Q3, Q4, Q5, Q6, Q7, Q8, Q9, Q10, Q11]), "radius" : 0.5 * mm, "tangentPropagation" : true, "allowEdgeOverflow" : false});
        }
    });
